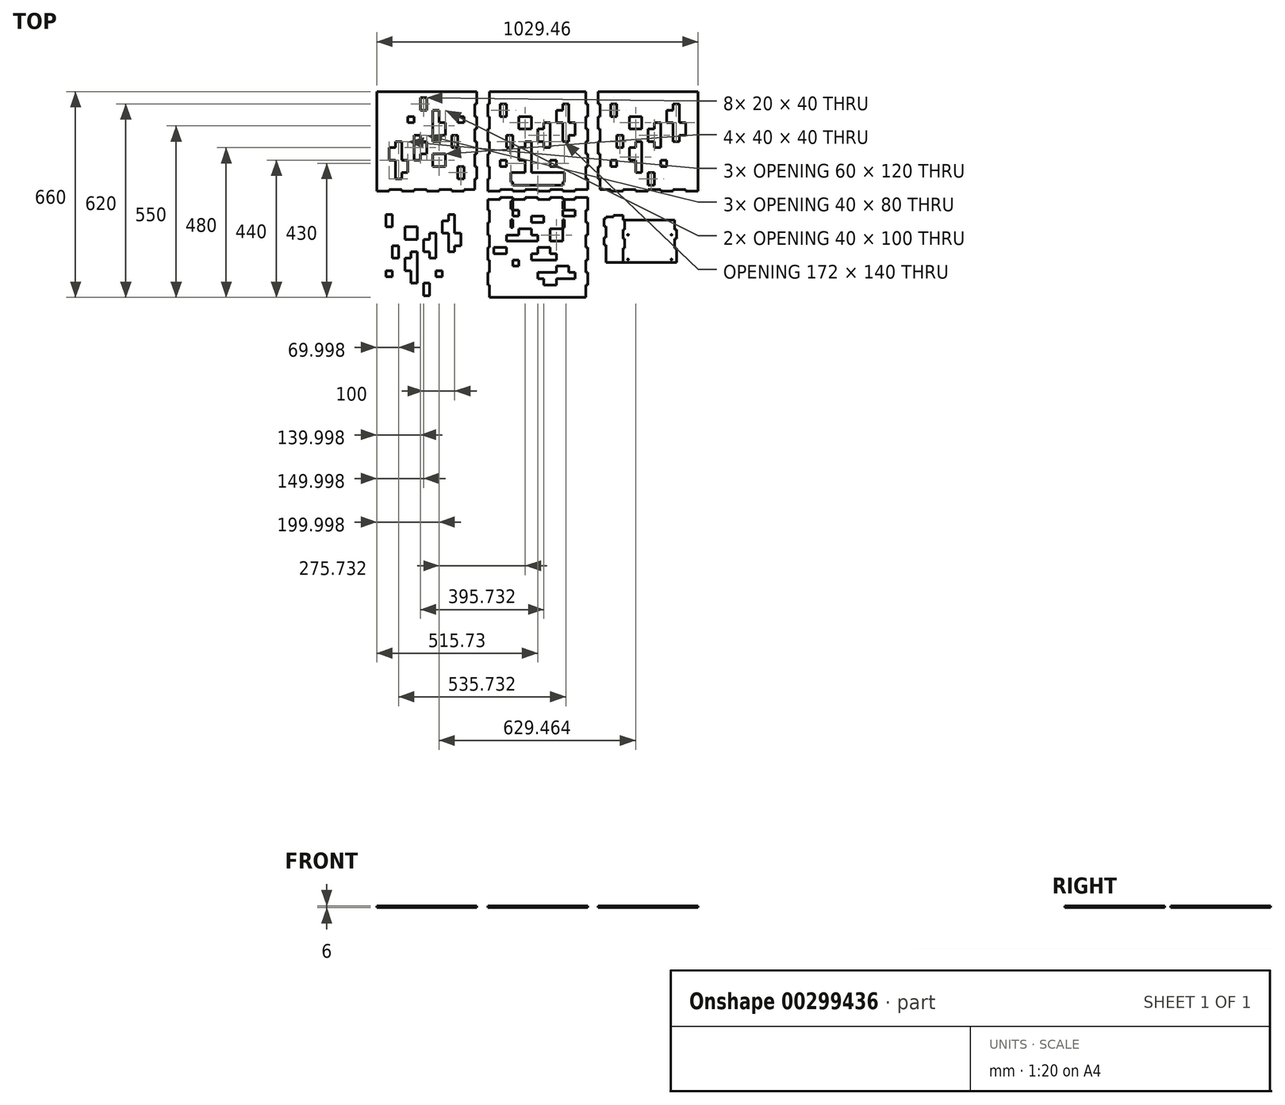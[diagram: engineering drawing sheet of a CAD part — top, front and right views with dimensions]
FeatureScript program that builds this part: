
annotation { "Feature Type Name" : "Feature", "Feature Type Description" : "" }
export const myFeature = defineFeature(function(context is Context, id is Id, definition is map)
    precondition{}
    {
        {
            var Q0;
            Q0=qCreatedBy(makeId("Top.planeOp"),FACE);
            var sketch = newSketch(context, id + "F0", { "sketchPlane" : qUnion([Q0])});
            skLineSegment(sketch, "E0.bottom", {"start": v(0, 0) * mm, "end": v(40, 0) * mm});
            skLineSegment(sketch, "E0.top", {"start": v(6, 320) * mm, "end": v(314, 320) * mm});
            skLineSegment(sketch, "E0.left", {"start": v(0, 0) * mm, "end": v(0, 40) * mm});
            skLineSegment(sketch, "E0.right", {"start": v(320, 6) * mm, "end": v(320, 40) * mm});
            skLineSegment(sketch, "E1.top", {"start": v(40, 6) * mm, "end": v(80, 6) * mm});
            skLineSegment(sketch, "E1.left", {"start": v(40, 0) * mm, "end": v(40, 6) * mm});
            skLineSegment(sketch, "E1.right", {"start": v(80, 0) * mm, "end": v(80, 6) * mm});
            skLineSegment(sketch, "E2.bottom", {"start": v(320, 40) * mm, "end": v(314, 40) * mm});
            skLineSegment(sketch, "E2.top", {"start": v(320, 80) * mm, "end": v(314, 80) * mm});
            skLineSegment(sketch, "E2.right", {"start": v(314, 40) * mm, "end": v(314, 80) * mm});
            skLineSegment(sketch, "E3.0.1.0", {"start": v(320, 160) * mm, "end": v(314, 160) * mm});
            skLineSegment(sketch, "E3.0.1.1", {"start": v(314, 120) * mm, "end": v(314, 160) * mm});
            skLineSegment(sketch, "E3.0.1.2", {"start": v(320, 120) * mm, "end": v(314, 120) * mm});
            skLineSegment(sketch, "E3.0.2.0", {"start": v(320, 240) * mm, "end": v(314, 240) * mm});
            skLineSegment(sketch, "E3.0.2.1", {"start": v(314, 200) * mm, "end": v(314, 240) * mm});
            skLineSegment(sketch, "E3.0.2.2", {"start": v(320, 200) * mm, "end": v(314, 200) * mm});
            skLineSegment(sketch, "E3.0.3.1", {"start": v(314, 280) * mm, "end": v(314, 320) * mm});
            skLineSegment(sketch, "E3.0.3.2", {"start": v(320, 280) * mm, "end": v(314, 280) * mm});
            skLineSegment(sketch, "E3.direction1", {"start": v(314, 80) * mm, "end": v(335.08, 80) * mm, "construction": true});
            skLineSegment(sketch, "E3.direction2", {"start": v(314, 80) * mm, "end": v(314, 160) * mm, "construction": true});
            skLineSegment(sketch, "E4.trimOffspring", {"start": v(320, 80) * mm, "end": v(320, 120) * mm});
            skLineSegment(sketch, "E5.trimOffspring", {"start": v(320, 160) * mm, "end": v(320, 200) * mm});
            skLineSegment(sketch, "E6.trimOffspring", {"start": v(320, 240) * mm, "end": v(320, 280) * mm});
            skLineSegment(sketch, "E7.1.0.0", {"start": v(80, 0) * mm, "end": v(120, 0) * mm});
            skLineSegment(sketch, "E7.1.0.1", {"start": v(120, 6) * mm, "end": v(160, 6) * mm});
            skLineSegment(sketch, "E7.1.0.2", {"start": v(120, 0) * mm, "end": v(120, 6) * mm});
            skLineSegment(sketch, "E7.1.0.3", {"start": v(160, 0) * mm, "end": v(160, 6) * mm});
            skLineSegment(sketch, "E7.2.0.0", {"start": v(160, 0) * mm, "end": v(200, 0) * mm});
            skLineSegment(sketch, "E7.2.0.1", {"start": v(200, 6) * mm, "end": v(240, 6) * mm});
            skLineSegment(sketch, "E7.2.0.2", {"start": v(200, 0) * mm, "end": v(200, 6) * mm});
            skLineSegment(sketch, "E7.2.0.3", {"start": v(240, 0) * mm, "end": v(240, 6) * mm});
            skLineSegment(sketch, "E7.3.0.0", {"start": v(240, 0) * mm, "end": v(280, 0) * mm});
            skLineSegment(sketch, "E7.3.0.1", {"start": v(280, 6) * mm, "end": v(320, 6) * mm});
            skLineSegment(sketch, "E7.3.0.2", {"start": v(280, 0) * mm, "end": v(280, 6) * mm});
            skLineSegment(sketch, "E7.direction1", {"start": v(0, 0) * mm, "end": v(80, 0) * mm, "construction": true});
            skLineSegment(sketch, "E8.bottom", {"start": v(0, 40) * mm, "end": v(6, 40) * mm});
            skLineSegment(sketch, "E8.top", {"start": v(0, 80) * mm, "end": v(6, 80) * mm});
            skLineSegment(sketch, "E8.right", {"start": v(6, 40) * mm, "end": v(6, 80) * mm});
            skLineSegment(sketch, "E9.0.1.0", {"start": v(0, 160) * mm, "end": v(6, 160) * mm});
            skLineSegment(sketch, "E9.0.1.1", {"start": v(6, 120) * mm, "end": v(6, 160) * mm});
            skLineSegment(sketch, "E9.0.1.2", {"start": v(0, 120) * mm, "end": v(6, 120) * mm});
            skLineSegment(sketch, "E9.0.2.0", {"start": v(0, 240) * mm, "end": v(6, 240) * mm});
            skLineSegment(sketch, "E9.0.2.1", {"start": v(6, 200) * mm, "end": v(6, 240) * mm});
            skLineSegment(sketch, "E9.0.2.2", {"start": v(0, 200) * mm, "end": v(6, 200) * mm});
            skLineSegment(sketch, "E9.0.3.1", {"start": v(6, 280) * mm, "end": v(6, 320) * mm});
            skLineSegment(sketch, "E9.0.3.2", {"start": v(0, 280) * mm, "end": v(6, 280) * mm});
            skLineSegment(sketch, "E9.direction1", {"start": v(0, 80) * mm, "end": v(25, 80) * mm, "construction": true});
            skLineSegment(sketch, "E9.direction2", {"start": v(0, 80) * mm, "end": v(0, 120) * mm, "construction": true});
            skLineSegment(sketch, "E10.trimOffspring", {"start": v(0, 240) * mm, "end": v(0, 280) * mm});
            skLineSegment(sketch, "E11.trimOffspring", {"start": v(0, 160) * mm, "end": v(0, 200) * mm});
            skLineSegment(sketch, "E12.trimOffspring", {"start": v(0, 80) * mm, "end": v(0, 120) * mm});
            skSolve(sketch);
        }
        {
            var Q0;
            Q0 = qSketchRegion(id + "F0", true);
            extrude(context, id + "F1", {"entities" : qUnion([Q0]), "depth" : 6 * mm});
        }
        {
            var Q0;
            Q0=makeQuery(id+"F1.opExtrude","SWEPT_BODY",BODY,{"disambiguationData":[OSD([sQuery(id+"F0.wireOp",EDGE,"E0.bottom"),sQuery(id+"F0.wireOp",EDGE,"E0.top"),sQuery(id+"F0.wireOp",EDGE,"E0.left"),sQuery(id+"F0.wireOp",EDGE,"E0.right"),sQuery(id+"F0.wireOp",EDGE,"E1.top"),sQuery(id+"F0.wireOp",EDGE,"E1.left"),sQuery(id+"F0.wireOp",EDGE,"E1.right"),sQuery(id+"F0.wireOp",EDGE,"E2.bottom"),sQuery(id+"F0.wireOp",EDGE,"E2.top"),sQuery(id+"F0.wireOp",EDGE,"E2.right"),sQuery(id+"F0.wireOp",EDGE,"E3.0.1.0"),sQuery(id+"F0.wireOp",EDGE,"E3.0.1.1"),sQuery(id+"F0.wireOp",EDGE,"E3.0.1.2"),sQuery(id+"F0.wireOp",EDGE,"E3.0.2.0"),sQuery(id+"F0.wireOp",EDGE,"E3.0.2.1"),sQuery(id+"F0.wireOp",EDGE,"E3.0.2.2"),sQuery(id+"F0.wireOp",EDGE,"E3.0.3.1"),sQuery(id+"F0.wireOp",EDGE,"E3.0.3.2"),sQuery(id+"F0.wireOp",EDGE,"E4.trimOffspring"),sQuery(id+"F0.wireOp",EDGE,"E5.trimOffspring"),sQuery(id+"F0.wireOp",EDGE,"E6.trimOffspring"),sQuery(id+"F0.wireOp",EDGE,"E7.1.0.0"),sQuery(id+"F0.wireOp",EDGE,"E7.1.0.1"),sQuery(id+"F0.wireOp",EDGE,"E7.1.0.2"),sQuery(id+"F0.wireOp",EDGE,"E7.1.0.3"),sQuery(id+"F0.wireOp",EDGE,"E7.2.0.0"),sQuery(id+"F0.wireOp",EDGE,"E7.2.0.1"),sQuery(id+"F0.wireOp",EDGE,"E7.2.0.2"),sQuery(id+"F0.wireOp",EDGE,"E7.2.0.3"),sQuery(id+"F0.wireOp",EDGE,"E7.3.0.0"),sQuery(id+"F0.wireOp",EDGE,"E7.3.0.1"),sQuery(id+"F0.wireOp",EDGE,"E7.3.0.2"),sQuery(id+"F0.wireOp",EDGE,"E8.bottom"),sQuery(id+"F0.wireOp",EDGE,"E8.top"),sQuery(id+"F0.wireOp",EDGE,"E8.right"),sQuery(id+"F0.wireOp",EDGE,"E9.0.1.0"),sQuery(id+"F0.wireOp",EDGE,"E9.0.1.1"),sQuery(id+"F0.wireOp",EDGE,"E9.0.1.2"),sQuery(id+"F0.wireOp",EDGE,"E9.0.2.0"),sQuery(id+"F0.wireOp",EDGE,"E9.0.2.1"),sQuery(id+"F0.wireOp",EDGE,"E9.0.2.2"),sQuery(id+"F0.wireOp",EDGE,"E9.0.3.1"),sQuery(id+"F0.wireOp",EDGE,"E9.0.3.2"),sQuery(id+"F0.wireOp",EDGE,"E10.trimOffspring"),sQuery(id+"F0.wireOp",EDGE,"E11.trimOffspring"),sQuery(id+"F0.wireOp",EDGE,"E12.trimOffspring")])]});
            var Q1;
            Q1=makeQuery(id+"F1.opExtrude","SWEPT_EDGE",EDGE,{"disambiguationData":[OSD([sQuery(id+"F0.wireOp",EDGE,"E0.bottom"),sQuery(id+"F0.wireOp",EDGE,"E0.left")])]});
            transform(context, id + "F2", {"entities" : qUnion([Q0]), "transformType" : TransformType.ROTATION, "transformAxis" : qUnion([Q1]), "angle" : 180 * degree, "makeCopy" : true});
        }
        {
            var Q0;
            Q0=makeQuery(id+"F2.opPattern","COPY",BODY,{"derivedFrom":makeQuery(id+"F1.opExtrude","SWEPT_BODY",BODY,{"disambiguationData":[OSD([sQuery(id+"F0.wireOp",EDGE,"E0.bottom"),sQuery(id+"F0.wireOp",EDGE,"E0.top"),sQuery(id+"F0.wireOp",EDGE,"E0.left"),sQuery(id+"F0.wireOp",EDGE,"E0.right"),sQuery(id+"F0.wireOp",EDGE,"E1.top"),sQuery(id+"F0.wireOp",EDGE,"E1.left"),sQuery(id+"F0.wireOp",EDGE,"E1.right"),sQuery(id+"F0.wireOp",EDGE,"E2.bottom"),sQuery(id+"F0.wireOp",EDGE,"E2.top"),sQuery(id+"F0.wireOp",EDGE,"E2.right"),sQuery(id+"F0.wireOp",EDGE,"E3.0.1.0"),sQuery(id+"F0.wireOp",EDGE,"E3.0.1.1"),sQuery(id+"F0.wireOp",EDGE,"E3.0.1.2"),sQuery(id+"F0.wireOp",EDGE,"E3.0.2.0"),sQuery(id+"F0.wireOp",EDGE,"E3.0.2.1"),sQuery(id+"F0.wireOp",EDGE,"E3.0.2.2"),sQuery(id+"F0.wireOp",EDGE,"E3.0.3.1"),sQuery(id+"F0.wireOp",EDGE,"E3.0.3.2"),sQuery(id+"F0.wireOp",EDGE,"E4.trimOffspring"),sQuery(id+"F0.wireOp",EDGE,"E5.trimOffspring"),sQuery(id+"F0.wireOp",EDGE,"E6.trimOffspring"),sQuery(id+"F0.wireOp",EDGE,"E7.1.0.0"),sQuery(id+"F0.wireOp",EDGE,"E7.1.0.1"),sQuery(id+"F0.wireOp",EDGE,"E7.1.0.2"),sQuery(id+"F0.wireOp",EDGE,"E7.1.0.3"),sQuery(id+"F0.wireOp",EDGE,"E7.2.0.0"),sQuery(id+"F0.wireOp",EDGE,"E7.2.0.1"),sQuery(id+"F0.wireOp",EDGE,"E7.2.0.2"),sQuery(id+"F0.wireOp",EDGE,"E7.2.0.3"),sQuery(id+"F0.wireOp",EDGE,"E7.3.0.0"),sQuery(id+"F0.wireOp",EDGE,"E7.3.0.1"),sQuery(id+"F0.wireOp",EDGE,"E7.3.0.2"),sQuery(id+"F0.wireOp",EDGE,"E8.bottom"),sQuery(id+"F0.wireOp",EDGE,"E8.top"),sQuery(id+"F0.wireOp",EDGE,"E8.right"),sQuery(id+"F0.wireOp",EDGE,"E9.0.1.0"),sQuery(id+"F0.wireOp",EDGE,"E9.0.1.1"),sQuery(id+"F0.wireOp",EDGE,"E9.0.1.2"),sQuery(id+"F0.wireOp",EDGE,"E9.0.2.0"),sQuery(id+"F0.wireOp",EDGE,"E9.0.2.1"),sQuery(id+"F0.wireOp",EDGE,"E9.0.2.2"),sQuery(id+"F0.wireOp",EDGE,"E9.0.3.1"),sQuery(id+"F0.wireOp",EDGE,"E9.0.3.2"),sQuery(id+"F0.wireOp",EDGE,"E10.trimOffspring"),sQuery(id+"F0.wireOp",EDGE,"E11.trimOffspring"),sQuery(id+"F0.wireOp",EDGE,"E12.trimOffspring")])]}),"instanceName":"1"});
            transform(context, id + "F3", {"entities" : qUnion([Q0]), "transformType" : TransformType.TRANSLATION_3D, "dx" : 320 * mm, "dy" : -20 * mm, "dz" : 0 * mm, "makeCopy" : false});
        }
        {
            var Q0;
            Q0=makeQuery(id+"F1.opExtrude","CAP_FACE",FACE,{"disambiguationData":[OSD([sQuery(id+"F0.wireOp",EDGE,"E0.bottom"),sQuery(id+"F0.wireOp",EDGE,"E0.top"),sQuery(id+"F0.wireOp",EDGE,"E0.left"),sQuery(id+"F0.wireOp",EDGE,"E0.right"),sQuery(id+"F0.wireOp",EDGE,"E1.top"),sQuery(id+"F0.wireOp",EDGE,"E1.left"),sQuery(id+"F0.wireOp",EDGE,"E1.right"),sQuery(id+"F0.wireOp",EDGE,"E2.bottom"),sQuery(id+"F0.wireOp",EDGE,"E2.top"),sQuery(id+"F0.wireOp",EDGE,"E2.right"),sQuery(id+"F0.wireOp",EDGE,"E3.0.1.0"),sQuery(id+"F0.wireOp",EDGE,"E3.0.1.1"),sQuery(id+"F0.wireOp",EDGE,"E3.0.1.2"),sQuery(id+"F0.wireOp",EDGE,"E3.0.2.0"),sQuery(id+"F0.wireOp",EDGE,"E3.0.2.1"),sQuery(id+"F0.wireOp",EDGE,"E3.0.2.2"),sQuery(id+"F0.wireOp",EDGE,"E3.0.3.1"),sQuery(id+"F0.wireOp",EDGE,"E3.0.3.2"),sQuery(id+"F0.wireOp",EDGE,"E4.trimOffspring"),sQuery(id+"F0.wireOp",EDGE,"E5.trimOffspring"),sQuery(id+"F0.wireOp",EDGE,"E6.trimOffspring"),sQuery(id+"F0.wireOp",EDGE,"E7.1.0.0"),sQuery(id+"F0.wireOp",EDGE,"E7.1.0.1"),sQuery(id+"F0.wireOp",EDGE,"E7.1.0.2"),sQuery(id+"F0.wireOp",EDGE,"E7.1.0.3"),sQuery(id+"F0.wireOp",EDGE,"E7.2.0.0"),sQuery(id+"F0.wireOp",EDGE,"E7.2.0.1"),sQuery(id+"F0.wireOp",EDGE,"E7.2.0.2"),sQuery(id+"F0.wireOp",EDGE,"E7.2.0.3"),sQuery(id+"F0.wireOp",EDGE,"E7.3.0.0"),sQuery(id+"F0.wireOp",EDGE,"E7.3.0.1"),sQuery(id+"F0.wireOp",EDGE,"E7.3.0.2"),sQuery(id+"F0.wireOp",EDGE,"E8.bottom"),sQuery(id+"F0.wireOp",EDGE,"E8.top"),sQuery(id+"F0.wireOp",EDGE,"E8.right"),sQuery(id+"F0.wireOp",EDGE,"E9.0.1.0"),sQuery(id+"F0.wireOp",EDGE,"E9.0.1.1"),sQuery(id+"F0.wireOp",EDGE,"E9.0.1.2"),sQuery(id+"F0.wireOp",EDGE,"E9.0.2.0"),sQuery(id+"F0.wireOp",EDGE,"E9.0.2.1"),sQuery(id+"F0.wireOp",EDGE,"E9.0.2.2"),sQuery(id+"F0.wireOp",EDGE,"E9.0.3.1"),sQuery(id+"F0.wireOp",EDGE,"E9.0.3.2"),sQuery(id+"F0.wireOp",EDGE,"E10.trimOffspring"),sQuery(id+"F0.wireOp",EDGE,"E11.trimOffspring"),sQuery(id+"F0.wireOp",EDGE,"E12.trimOffspring")])],"isStart":false});
            var sketch = newSketch(context, id + "F4", { "sketchPlane" : qUnion([Q0])});
            skLineSegment(sketch, "E13", {"start": v(160, 320) * mm, "end": v(160, 6) * mm, "construction": true});
            skLineSegment(sketch, "E14.bottom", {"start": v(74, 60) * mm, "end": v(80, 60) * mm});
            skLineSegment(sketch, "E14.top", {"start": v(74, 30) * mm, "end": v(80, 30) * mm});
            skLineSegment(sketch, "E14.left", {"start": v(74, 60) * mm, "end": v(74, 30) * mm});
            skLineSegment(sketch, "E14.right", {"start": v(80, 60) * mm, "end": v(80, 30) * mm});
            skLineSegment(sketch, "E15.MirrorCS", {"start": v(246, 60) * mm, "end": v(240, 60) * mm});
            skLineSegment(sketch, "E16.MirrorCS", {"start": v(246, 60) * mm, "end": v(246, 30) * mm});
            skLineSegment(sketch, "E17.MirrorCS", {"start": v(246, 30) * mm, "end": v(240, 30) * mm});
            skLineSegment(sketch, "E18.MirrorCS", {"start": v(240, 60) * mm, "end": v(240, 30) * mm});
            skLineSegment(sketch, "E19.bottom", {"start": v(74, -31) * mm, "end": v(80, -31) * mm});
            skLineSegment(sketch, "E19.top", {"start": v(74, -56) * mm, "end": v(80, -56) * mm});
            skLineSegment(sketch, "E19.left", {"start": v(74, -31) * mm, "end": v(74, -56) * mm});
            skLineSegment(sketch, "E19.right", {"start": v(80, -31) * mm, "end": v(80, -56) * mm});
            skLineSegment(sketch, "E20", {"start": v(6, -166) * mm, "end": v(314, -166) * mm, "construction": true});
            skLineSegment(sketch, "E21.0.1.0", {"start": v(74, -116) * mm, "end": v(80, -116) * mm});
            skLineSegment(sketch, "E21.0.1.1", {"start": v(80, -91) * mm, "end": v(80, -116) * mm});
            skLineSegment(sketch, "E21.0.1.2", {"start": v(74, -91) * mm, "end": v(80, -91) * mm});
            skLineSegment(sketch, "E21.0.1.3", {"start": v(74, -91) * mm, "end": v(74, -116) * mm});
            skLineSegment(sketch, "E21.direction1", {"start": v(74, -56) * mm, "end": v(103, -56) * mm, "construction": true});
            skLineSegment(sketch, "E21.direction2", {"start": v(74, -56) * mm, "end": v(74, -116) * mm, "construction": true});
            skLineSegment(sketch, "E22.MirrorCS", {"start": v(246, -116) * mm, "end": v(240, -116) * mm});
            skLineSegment(sketch, "E23.MirrorCS", {"start": v(246, -91) * mm, "end": v(240, -91) * mm});
            skLineSegment(sketch, "E24.MirrorCS", {"start": v(240, -91) * mm, "end": v(240, -116) * mm});
            skLineSegment(sketch, "E25.MirrorCS", {"start": v(246, -91) * mm, "end": v(246, -116) * mm});
            skLineSegment(sketch, "E26.MirrorCS", {"start": v(246, -56) * mm, "end": v(240, -56) * mm});
            skLineSegment(sketch, "E27.MirrorCS", {"start": v(246, -31) * mm, "end": v(240, -31) * mm});
            skLineSegment(sketch, "E28.MirrorCS", {"start": v(246, -31) * mm, "end": v(246, -56) * mm});
            skLineSegment(sketch, "E29.MirrorCS", {"start": v(240, -31) * mm, "end": v(240, -56) * mm});
            skLineSegment(sketch, "E30.bottom", {"start": v(80, 60) * mm, "end": v(240, 60) * mm});
            skLineSegment(sketch, "E30.top", {"start": v(80, 20) * mm, "end": v(240, 20) * mm});
            skLineSegment(sketch, "E30.left", {"start": v(80, 60) * mm, "end": v(80, 20) * mm});
            skLineSegment(sketch, "E30.right", {"start": v(240, 60) * mm, "end": v(240, 20) * mm});
            skSolve(sketch);
        }
        {
            var Q0;
            Q0 = qSketchRegion(id + "F4", true);
            extrude(context, id + "F5", {"entities" : qUnion([Q0]), "operationType" : NewBodyOperationType.REMOVE, "endBound" : BoundingType.THROUGH_ALL, "oppositeDirection" : true, "depth" : 25 * mm});
        }
        {
            var Q0;
            Q0=makeQuery(id+"F4.imprint","IMPRINT",FACE,{"disambiguationData":[TD([[makeQuery(id+"F4.imprint","IMPRINT",EDGE,{"derivedFrom":sQuery(id+"F4.wireOp",EDGE,"E19.bottom")}),-1.0]])]});
            var Q1;
            Q1=makeQuery(id+"F4.imprint","IMPRINT",FACE,{"disambiguationData":[TD([[makeQuery(id+"F4.imprint","IMPRINT",EDGE,{"derivedFrom":sQuery(id+"F4.wireOp",EDGE,"E26.MirrorCS")}),-1.0]])]});
            var Q2;
            Q2=makeQuery(id+"F4.imprint","IMPRINT",FACE,{"disambiguationData":[TD([[makeQuery(id+"F4.imprint","IMPRINT",EDGE,{"derivedFrom":sQuery(id+"F4.wireOp",EDGE,"E21.0.1.0")}),1.0]])]});
            var Q3;
            Q3=makeQuery(id+"F4.imprint","IMPRINT",FACE,{"disambiguationData":[TD([[makeQuery(id+"F4.imprint","IMPRINT",EDGE,{"derivedFrom":sQuery(id+"F4.wireOp",EDGE,"E22.MirrorCS")}),-1.0]])]});
            extrude(context, id + "F6", {"entities" : qUnion([Q0, Q1, Q2, Q3]), "operationType" : NewBodyOperationType.REMOVE, "endBound" : BoundingType.THROUGH_ALL, "oppositeDirection" : true, "depth" : 25 * mm});
        }
        {
            var Q0;
            Q0=qCreatedBy(makeId("Top.planeOp"),FACE);
            var sketch = newSketch(context, id + "F7", { "sketchPlane" : qUnion([Q0])});
            skLineSegment(sketch, "E31.bottom", {"start": v(378.9, -82.37) * mm, "end": v(402.9, -82.37) * mm});
            skLineSegment(sketch, "E31.top", {"start": v(378.9, -227.37) * mm, "end": v(432.9, -227.37) * mm});
            skLineSegment(sketch, "E31.left", {"start": v(378.9, -82.37) * mm, "end": v(378.9, -87.37) * mm});
            skLineSegment(sketch, "E31.right", {"start": v(432.9, -76.37) * mm, "end": v(432.9, -92.37) * mm});
            skLineSegment(sketch, "E32.bottom", {"start": v(378.9, -87.37) * mm, "end": v(372.9, -87.37) * mm});
            skLineSegment(sketch, "E32.top", {"start": v(378.9, -112.37) * mm, "end": v(372.9, -112.37) * mm});
            skLineSegment(sketch, "E32.right", {"start": v(372.9, -87.37) * mm, "end": v(372.9, -112.37) * mm});
            skLineSegment(sketch, "E33.top", {"start": v(432.9, -76.37) * mm, "end": v(402.9, -76.37) * mm});
            skLineSegment(sketch, "E33.right", {"start": v(402.9, -82.37) * mm, "end": v(402.9, -76.37) * mm});
            skLineSegment(sketch, "E34.0.1.0", {"start": v(378.9, -172.37) * mm, "end": v(372.9, -172.37) * mm});
            skLineSegment(sketch, "E34.0.1.1", {"start": v(372.9, -147.37) * mm, "end": v(372.9, -172.37) * mm});
            skLineSegment(sketch, "E34.0.1.2", {"start": v(378.9, -147.37) * mm, "end": v(372.9, -147.37) * mm});
            skLineSegment(sketch, "E34.direction1", {"start": v(372.9, -112.37) * mm, "end": v(386.62, -112.37) * mm, "construction": true});
            skLineSegment(sketch, "E34.direction2", {"start": v(372.9, -112.37) * mm, "end": v(372.9, -172.37) * mm, "construction": true});
            skLineSegment(sketch, "E35.trimOffspring", {"start": v(378.9, -112.37) * mm, "end": v(378.9, -147.37) * mm});
            skLineSegment(sketch, "E36.trimOffspring", {"start": v(378.9, -172.37) * mm, "end": v(378.9, -227.37) * mm});
            skLineSegment(sketch, "E37.bottom", {"start": v(432.9, -92.37) * mm, "end": v(438.9, -92.37) * mm});
            skLineSegment(sketch, "E37.top", {"start": v(432.9, -122.37) * mm, "end": v(438.9, -122.37) * mm});
            skLineSegment(sketch, "E37.right", {"start": v(438.9, -92.37) * mm, "end": v(438.9, -122.37) * mm});
            skLineSegment(sketch, "E38.0.1.0", {"start": v(432.9, -152.37) * mm, "end": v(438.9, -152.37) * mm});
            skLineSegment(sketch, "E38.0.1.1", {"start": v(438.9, -152.37) * mm, "end": v(438.9, -182.37) * mm});
            skLineSegment(sketch, "E38.0.1.2", {"start": v(432.9, -182.37) * mm, "end": v(438.9, -182.37) * mm});
            skLineSegment(sketch, "E38.direction2", {"start": v(432.9, -122.37) * mm, "end": v(432.9, -152.37) * mm, "construction": true});
            skLineSegment(sketch, "E39.trimOffspring", {"start": v(432.9, -182.37) * mm, "end": v(432.9, -227.37) * mm});
            skLineSegment(sketch, "E40.trimOffspring", {"start": v(432.9, -122.37) * mm, "end": v(432.9, -152.37) * mm});
            skLineSegment(sketch, "E41", {"start": v(432.9, -227.37) * mm, "end": v(518.9, -227.37) * mm});
            skLineSegment(sketch, "E42", {"start": v(518.9, -92.37) * mm, "end": v(518.9, -227.37) * mm, "construction": true});
            skLineSegment(sketch, "E43.MirrorCS", {"start": v(604.9, -182.37) * mm, "end": v(598.9, -182.37) * mm});
            skLineSegment(sketch, "E44.MirrorCS", {"start": v(604.9, -122.37) * mm, "end": v(598.9, -122.37) * mm});
            skLineSegment(sketch, "E45.MirrorCS", {"start": v(604.9, -152.37) * mm, "end": v(598.9, -152.37) * mm});
            skLineSegment(sketch, "E46.MirrorCS", {"start": v(604.9, -122.37) * mm, "end": v(604.9, -152.37) * mm});
            skLineSegment(sketch, "E47.MirrorCS", {"start": v(598.9, -152.37) * mm, "end": v(598.9, -182.37) * mm});
            skLineSegment(sketch, "E48.MirrorCS", {"start": v(604.9, -182.37) * mm, "end": v(604.9, -227.37) * mm});
            skLineSegment(sketch, "E49.MirrorCS", {"start": v(604.9, -122.37) * mm, "end": v(604.9, -152.37) * mm, "construction": true});
            skLineSegment(sketch, "E50.MirrorCS", {"start": v(598.9, -92.37) * mm, "end": v(598.9, -122.37) * mm});
            skLineSegment(sketch, "E51.MirrorCS", {"start": v(604.9, -227.37) * mm, "end": v(518.9, -227.37) * mm});
            skPoint(sketch, "E52", {"position": v(449.2, -139.37) * mm});
            skPoint(sketch, "E53.MirrorP", {"position": v(588.6, -139.37) * mm});
            skPoint(sketch, "E54", {"position": v(449.2, -218.37) * mm});
            skPoint(sketch, "E55.MirrorP", {"position": v(588.6, -218.37) * mm});
            skLineSegment(sketch, "E56", {"start": v(438.9, -92.37) * mm, "end": v(598.9, -92.37) * mm});
            skSolve(sketch);
        }
        {
            var Q0;
            Q0=makeQuery(id+"F7.imprint","IMPRINT",FACE,{"disambiguationData":[TD([[makeQuery(id+"F7.imprint","IMPRINT",EDGE,{"derivedFrom":sQuery(id+"F7.wireOp",EDGE,"E31.bottom")}),-1.0]])]});
            extrude(context, id + "F8", {"entities" : qUnion([Q0]), "depth" : 6 * mm});
        }
        {
            var Q0;
            Q0=makeQuery(id+"F7.imprint","IMPRINT",FACE,{"disambiguationData":[TD([[makeQuery(id+"F7.imprint","IMPRINT",EDGE,{"derivedFrom":sQuery(id+"F7.wireOp",EDGE,"E37.top")}),-1.0]])]});
            extrude(context, id + "F9", {"entities" : qUnion([Q0]), "depth" : 6 * mm});
        }
        {
            var Q0;
            Q0=sQuery(id+"F7.wireOp",VERTEX,"E52");
            var Q1;
            Q1=sQuery(id+"F7.wireOp",VERTEX,"E53.MirrorP");
            var Q2;
            Q2=sQuery(id+"F7.wireOp",VERTEX,"E54");
            var Q3;
            Q3=sQuery(id+"F7.wireOp",VERTEX,"E55.MirrorP");
            var Q4;
            Q4=makeQuery(id+"F9.opExtrude","SWEPT_BODY",BODY,{"disambiguationData":[OSD([sQuery(id+"F7.wireOp",EDGE,"E31.right"),sQuery(id+"F7.wireOp",EDGE,"E37.bottom"),sQuery(id+"F7.wireOp",EDGE,"E37.top"),sQuery(id+"F7.wireOp",EDGE,"E37.right"),sQuery(id+"F7.wireOp",EDGE,"E38.0.1.0"),sQuery(id+"F7.wireOp",EDGE,"E38.0.1.1"),sQuery(id+"F7.wireOp",EDGE,"E38.0.1.2"),sQuery(id+"F7.wireOp",EDGE,"E39.trimOffspring"),sQuery(id+"F7.wireOp",EDGE,"E40.trimOffspring"),sQuery(id+"F7.wireOp",EDGE,"jgh2MYiH-jTgE-0Iw7-kaac-s1TBbCvIartK"),sQuery(id+"F7.wireOp",EDGE,"E41"),sQuery(id+"F7.wireOp",EDGE,"de06030a-5946-498d-ad5b-0ab8e06975840.MirrorCS"),sQuery(id+"F7.wireOp",EDGE,"E43.MirrorCS"),sQuery(id+"F7.wireOp",EDGE,"E44.MirrorCS"),sQuery(id+"F7.wireOp",EDGE,"e7224b58-42de-4460-80b3-c9ff548c79182.MirrorCS"),sQuery(id+"F7.wireOp",EDGE,"E45.MirrorCS"),sQuery(id+"F7.wireOp",EDGE,"E46.MirrorCS"),sQuery(id+"F7.wireOp",EDGE,"E47.MirrorCS"),sQuery(id+"F7.wireOp",EDGE,"E48.MirrorCS"),sQuery(id+"F7.wireOp",EDGE,"e7224b58-42de-4460-80b3-c9ff548c79189.MirrorCS"),sQuery(id+"F7.wireOp",EDGE,"E50.MirrorCS"),sQuery(id+"F7.wireOp",EDGE,"E51.MirrorCS")])]});
            hole(context, id + "F10", {"style" : HoleStyle.SIMPLE, "endStyle" : HoleEndStyle.THROUGH, "oppositeDirection" : true, "standardTappedOrClearance" : lookupTablePath({ "standard" : "ISO", "fit" : "Normal", "size" : "M3", "type" : "Clearance" }), "standardBlindInLast" : lookupTablePath({ "fit" : "Standard", "standard" : "ISO", "size" : "M3", "type" : "Clearance" }), "holeDiameter" : 3.3 * mm, "tappedDepth" : 6 * mm, "tapClearance" : 3, "locations" : qUnion([Q0, Q1, Q2, Q3]), "scope" : qUnion([Q4])});
        }
        {
            var Q0;
            Q0=makeQuery(id+"F1.opExtrude","CAP_FACE",FACE,{"disambiguationData":[OSD([sQuery(id+"F0.wireOp",EDGE,"E0.bottom"),sQuery(id+"F0.wireOp",EDGE,"E0.top"),sQuery(id+"F0.wireOp",EDGE,"E0.left"),sQuery(id+"F0.wireOp",EDGE,"E0.right"),sQuery(id+"F0.wireOp",EDGE,"E1.top"),sQuery(id+"F0.wireOp",EDGE,"E1.left"),sQuery(id+"F0.wireOp",EDGE,"E1.right"),sQuery(id+"F0.wireOp",EDGE,"E2.bottom"),sQuery(id+"F0.wireOp",EDGE,"E2.top"),sQuery(id+"F0.wireOp",EDGE,"E2.right"),sQuery(id+"F0.wireOp",EDGE,"E3.0.1.0"),sQuery(id+"F0.wireOp",EDGE,"E3.0.1.1"),sQuery(id+"F0.wireOp",EDGE,"E3.0.1.2"),sQuery(id+"F0.wireOp",EDGE,"E3.0.2.0"),sQuery(id+"F0.wireOp",EDGE,"E3.0.2.1"),sQuery(id+"F0.wireOp",EDGE,"E3.0.2.2"),sQuery(id+"F0.wireOp",EDGE,"E3.0.3.1"),sQuery(id+"F0.wireOp",EDGE,"E3.0.3.2"),sQuery(id+"F0.wireOp",EDGE,"E4.trimOffspring"),sQuery(id+"F0.wireOp",EDGE,"E5.trimOffspring"),sQuery(id+"F0.wireOp",EDGE,"E6.trimOffspring"),sQuery(id+"F0.wireOp",EDGE,"E7.1.0.0"),sQuery(id+"F0.wireOp",EDGE,"E7.1.0.1"),sQuery(id+"F0.wireOp",EDGE,"E7.1.0.2"),sQuery(id+"F0.wireOp",EDGE,"E7.1.0.3"),sQuery(id+"F0.wireOp",EDGE,"E7.2.0.0"),sQuery(id+"F0.wireOp",EDGE,"E7.2.0.1"),sQuery(id+"F0.wireOp",EDGE,"E7.2.0.2"),sQuery(id+"F0.wireOp",EDGE,"E7.2.0.3"),sQuery(id+"F0.wireOp",EDGE,"E7.3.0.0"),sQuery(id+"F0.wireOp",EDGE,"E7.3.0.1"),sQuery(id+"F0.wireOp",EDGE,"E7.3.0.2"),sQuery(id+"F0.wireOp",EDGE,"E8.bottom"),sQuery(id+"F0.wireOp",EDGE,"E8.top"),sQuery(id+"F0.wireOp",EDGE,"E8.right"),sQuery(id+"F0.wireOp",EDGE,"E9.0.1.0"),sQuery(id+"F0.wireOp",EDGE,"E9.0.1.1"),sQuery(id+"F0.wireOp",EDGE,"E9.0.1.2"),sQuery(id+"F0.wireOp",EDGE,"E9.0.2.0"),sQuery(id+"F0.wireOp",EDGE,"E9.0.2.1"),sQuery(id+"F0.wireOp",EDGE,"E9.0.2.2"),sQuery(id+"F0.wireOp",EDGE,"E9.0.3.1"),sQuery(id+"F0.wireOp",EDGE,"E9.0.3.2"),sQuery(id+"F0.wireOp",EDGE,"E10.trimOffspring"),sQuery(id+"F0.wireOp",EDGE,"E11.trimOffspring"),sQuery(id+"F0.wireOp",EDGE,"E12.trimOffspring")])],"isStart":false});
            var sketch = newSketch(context, id + "F11", { "sketchPlane" : qUnion([Q0])});
            skPoint(sketch, "E57", {"position": v(20, 20) * mm});
            skPoint(sketch, "E58.0.1.0", {"position": v(20, 40) * mm});
            skPoint(sketch, "E58.0.2.0", {"position": v(20, 60) * mm});
            skPoint(sketch, "E58.0.3.0", {"position": v(20, 80) * mm});
            skPoint(sketch, "E58.0.4.0", {"position": v(20, 100) * mm});
            skPoint(sketch, "E58.0.5.0", {"position": v(20, 120) * mm});
            skPoint(sketch, "E58.0.6.0", {"position": v(20, 140) * mm});
            skPoint(sketch, "E58.0.7.0", {"position": v(20, 160) * mm});
            skPoint(sketch, "E58.0.8.0", {"position": v(20, 180) * mm});
            skPoint(sketch, "E58.0.9.0", {"position": v(20, 200) * mm});
            skPoint(sketch, "E58.0.10.0", {"position": v(20, 220) * mm});
            skPoint(sketch, "E58.0.11.0", {"position": v(20, 240) * mm});
            skPoint(sketch, "E58.0.12.0", {"position": v(20, 260) * mm});
            skPoint(sketch, "E58.0.13.0", {"position": v(20, 280) * mm});
            skPoint(sketch, "E58.1.0.0", {"position": v(40, 20) * mm});
            skPoint(sketch, "E58.1.1.0", {"position": v(40, 40) * mm});
            skPoint(sketch, "E58.1.2.0", {"position": v(40, 60) * mm});
            skPoint(sketch, "E58.1.3.0", {"position": v(40, 80) * mm});
            skPoint(sketch, "E58.1.4.0", {"position": v(40, 100) * mm});
            skPoint(sketch, "E58.1.5.0", {"position": v(40, 120) * mm});
            skPoint(sketch, "E58.1.6.0", {"position": v(40, 140) * mm});
            skPoint(sketch, "E58.1.7.0", {"position": v(40, 160) * mm});
            skPoint(sketch, "E58.1.8.0", {"position": v(40, 180) * mm});
            skPoint(sketch, "E58.1.9.0", {"position": v(40, 200) * mm});
            skPoint(sketch, "E58.1.10.0", {"position": v(40, 220) * mm});
            skPoint(sketch, "E58.1.11.0", {"position": v(40, 240) * mm});
            skPoint(sketch, "E58.1.12.0", {"position": v(40, 260) * mm});
            skPoint(sketch, "E58.1.13.0", {"position": v(40, 280) * mm});
            skPoint(sketch, "E58.2.0.0", {"position": v(60, 20) * mm});
            skPoint(sketch, "E58.2.1.0", {"position": v(60, 40) * mm});
            skPoint(sketch, "E58.2.2.0", {"position": v(60, 60) * mm});
            skPoint(sketch, "E58.2.3.0", {"position": v(60, 80) * mm});
            skPoint(sketch, "E58.2.4.0", {"position": v(60, 100) * mm});
            skPoint(sketch, "E58.2.5.0", {"position": v(60, 120) * mm});
            skPoint(sketch, "E58.2.6.0", {"position": v(60, 140) * mm});
            skPoint(sketch, "E58.2.7.0", {"position": v(60, 160) * mm});
            skPoint(sketch, "E58.2.8.0", {"position": v(60, 180) * mm});
            skPoint(sketch, "E58.2.9.0", {"position": v(60, 200) * mm});
            skPoint(sketch, "E58.2.10.0", {"position": v(60, 220) * mm});
            skPoint(sketch, "E58.2.11.0", {"position": v(60, 240) * mm});
            skPoint(sketch, "E58.2.12.0", {"position": v(60, 260) * mm});
            skPoint(sketch, "E58.2.13.0", {"position": v(60, 280) * mm});
            skPoint(sketch, "E58.3.0.0", {"position": v(80, 20) * mm});
            skPoint(sketch, "E58.3.1.0", {"position": v(80, 40) * mm});
            skPoint(sketch, "E58.3.2.0", {"position": v(80, 60) * mm});
            skPoint(sketch, "E58.3.3.0", {"position": v(80, 80) * mm});
            skPoint(sketch, "E58.3.4.0", {"position": v(80, 100) * mm});
            skPoint(sketch, "E58.3.5.0", {"position": v(80, 120) * mm});
            skPoint(sketch, "E58.3.6.0", {"position": v(80, 140) * mm});
            skPoint(sketch, "E58.3.7.0", {"position": v(80, 160) * mm});
            skPoint(sketch, "E58.3.8.0", {"position": v(80, 180) * mm});
            skPoint(sketch, "E58.3.9.0", {"position": v(80, 200) * mm});
            skPoint(sketch, "E58.3.10.0", {"position": v(80, 220) * mm});
            skPoint(sketch, "E58.3.11.0", {"position": v(80, 240) * mm});
            skPoint(sketch, "E58.3.12.0", {"position": v(80, 260) * mm});
            skPoint(sketch, "E58.3.13.0", {"position": v(80, 280) * mm});
            skPoint(sketch, "E58.4.0.0", {"position": v(100, 20) * mm});
            skPoint(sketch, "E58.4.1.0", {"position": v(100, 40) * mm});
            skPoint(sketch, "E58.4.2.0", {"position": v(100, 60) * mm});
            skPoint(sketch, "E58.4.3.0", {"position": v(100, 80) * mm});
            skPoint(sketch, "E58.4.4.0", {"position": v(100, 100) * mm});
            skPoint(sketch, "E58.4.5.0", {"position": v(100, 120) * mm});
            skPoint(sketch, "E58.4.6.0", {"position": v(100, 140) * mm});
            skPoint(sketch, "E58.4.7.0", {"position": v(100, 160) * mm});
            skPoint(sketch, "E58.4.8.0", {"position": v(100, 180) * mm});
            skPoint(sketch, "E58.4.9.0", {"position": v(100, 200) * mm});
            skPoint(sketch, "E58.4.10.0", {"position": v(100, 220) * mm});
            skPoint(sketch, "E58.4.11.0", {"position": v(100, 240) * mm});
            skPoint(sketch, "E58.4.12.0", {"position": v(100, 260) * mm});
            skPoint(sketch, "E58.4.13.0", {"position": v(100, 280) * mm});
            skPoint(sketch, "E58.5.0.0", {"position": v(120, 20) * mm});
            skPoint(sketch, "E58.5.1.0", {"position": v(120, 40) * mm});
            skPoint(sketch, "E58.5.2.0", {"position": v(120, 60) * mm});
            skPoint(sketch, "E58.5.3.0", {"position": v(120, 80) * mm});
            skPoint(sketch, "E58.5.4.0", {"position": v(120, 100) * mm});
            skPoint(sketch, "E58.5.5.0", {"position": v(120, 120) * mm});
            skPoint(sketch, "E58.5.6.0", {"position": v(120, 140) * mm});
            skPoint(sketch, "E58.5.7.0", {"position": v(120, 160) * mm});
            skPoint(sketch, "E58.5.8.0", {"position": v(120, 180) * mm});
            skPoint(sketch, "E58.5.9.0", {"position": v(120, 200) * mm});
            skPoint(sketch, "E58.5.10.0", {"position": v(120, 220) * mm});
            skPoint(sketch, "E58.5.11.0", {"position": v(120, 240) * mm});
            skPoint(sketch, "E58.5.12.0", {"position": v(120, 260) * mm});
            skPoint(sketch, "E58.5.13.0", {"position": v(120, 280) * mm});
            skPoint(sketch, "E58.6.0.0", {"position": v(140, 20) * mm});
            skPoint(sketch, "E58.6.1.0", {"position": v(140, 40) * mm});
            skPoint(sketch, "E58.6.2.0", {"position": v(140, 60) * mm});
            skPoint(sketch, "E58.6.3.0", {"position": v(140, 80) * mm});
            skPoint(sketch, "E58.6.4.0", {"position": v(140, 100) * mm});
            skPoint(sketch, "E58.6.5.0", {"position": v(140, 120) * mm});
            skPoint(sketch, "E58.6.6.0", {"position": v(140, 140) * mm});
            skPoint(sketch, "E58.6.7.0", {"position": v(140, 160) * mm});
            skPoint(sketch, "E58.6.8.0", {"position": v(140, 180) * mm});
            skPoint(sketch, "E58.6.9.0", {"position": v(140, 200) * mm});
            skPoint(sketch, "E58.6.10.0", {"position": v(140, 220) * mm});
            skPoint(sketch, "E58.6.11.0", {"position": v(140, 240) * mm});
            skPoint(sketch, "E58.6.12.0", {"position": v(140, 260) * mm});
            skPoint(sketch, "E58.6.13.0", {"position": v(140, 280) * mm});
            skPoint(sketch, "E58.7.0.0", {"position": v(160, 20) * mm});
            skPoint(sketch, "E58.7.1.0", {"position": v(160, 40) * mm});
            skPoint(sketch, "E58.7.2.0", {"position": v(160, 60) * mm});
            skPoint(sketch, "E58.7.3.0", {"position": v(160, 80) * mm});
            skPoint(sketch, "E58.7.4.0", {"position": v(160, 100) * mm});
            skPoint(sketch, "E58.7.5.0", {"position": v(160, 120) * mm});
            skPoint(sketch, "E58.7.6.0", {"position": v(160, 140) * mm});
            skPoint(sketch, "E58.7.7.0", {"position": v(160, 160) * mm});
            skPoint(sketch, "E58.7.8.0", {"position": v(160, 180) * mm});
            skPoint(sketch, "E58.7.9.0", {"position": v(160, 200) * mm});
            skPoint(sketch, "E58.7.10.0", {"position": v(160, 220) * mm});
            skPoint(sketch, "E58.7.11.0", {"position": v(160, 240) * mm});
            skPoint(sketch, "E58.7.12.0", {"position": v(160, 260) * mm});
            skPoint(sketch, "E58.7.13.0", {"position": v(160, 280) * mm});
            skPoint(sketch, "E58.8.0.0", {"position": v(180, 20) * mm});
            skPoint(sketch, "E58.8.1.0", {"position": v(180, 40) * mm});
            skPoint(sketch, "E58.8.2.0", {"position": v(180, 60) * mm});
            skPoint(sketch, "E58.8.3.0", {"position": v(180, 80) * mm});
            skPoint(sketch, "E58.8.4.0", {"position": v(180, 100) * mm});
            skPoint(sketch, "E58.8.5.0", {"position": v(180, 120) * mm});
            skPoint(sketch, "E58.8.6.0", {"position": v(180, 140) * mm});
            skPoint(sketch, "E58.8.7.0", {"position": v(180, 160) * mm});
            skPoint(sketch, "E58.8.8.0", {"position": v(180, 180) * mm});
            skPoint(sketch, "E58.8.9.0", {"position": v(180, 200) * mm});
            skPoint(sketch, "E58.8.10.0", {"position": v(180, 220) * mm});
            skPoint(sketch, "E58.8.11.0", {"position": v(180, 240) * mm});
            skPoint(sketch, "E58.8.12.0", {"position": v(180, 260) * mm});
            skPoint(sketch, "E58.8.13.0", {"position": v(180, 280) * mm});
            skPoint(sketch, "E58.9.0.0", {"position": v(200, 20) * mm});
            skPoint(sketch, "E58.9.1.0", {"position": v(200, 40) * mm});
            skPoint(sketch, "E58.9.2.0", {"position": v(200, 60) * mm});
            skPoint(sketch, "E58.9.3.0", {"position": v(200, 80) * mm});
            skPoint(sketch, "E58.9.4.0", {"position": v(200, 100) * mm});
            skPoint(sketch, "E58.9.5.0", {"position": v(200, 120) * mm});
            skPoint(sketch, "E58.9.6.0", {"position": v(200, 140) * mm});
            skPoint(sketch, "E58.9.7.0", {"position": v(200, 160) * mm});
            skPoint(sketch, "E58.9.8.0", {"position": v(200, 180) * mm});
            skPoint(sketch, "E58.9.9.0", {"position": v(200, 200) * mm});
            skPoint(sketch, "E58.9.10.0", {"position": v(200, 220) * mm});
            skPoint(sketch, "E58.9.11.0", {"position": v(200, 240) * mm});
            skPoint(sketch, "E58.9.12.0", {"position": v(200, 260) * mm});
            skPoint(sketch, "E58.9.13.0", {"position": v(200, 280) * mm});
            skPoint(sketch, "E58.10.0.0", {"position": v(220, 20) * mm});
            skPoint(sketch, "E58.10.1.0", {"position": v(220, 40) * mm});
            skPoint(sketch, "E58.10.2.0", {"position": v(220, 60) * mm});
            skPoint(sketch, "E58.10.3.0", {"position": v(220, 80) * mm});
            skPoint(sketch, "E58.10.4.0", {"position": v(220, 100) * mm});
            skPoint(sketch, "E58.10.5.0", {"position": v(220, 120) * mm});
            skPoint(sketch, "E58.10.6.0", {"position": v(220, 140) * mm});
            skPoint(sketch, "E58.10.7.0", {"position": v(220, 160) * mm});
            skPoint(sketch, "E58.10.8.0", {"position": v(220, 180) * mm});
            skPoint(sketch, "E58.10.9.0", {"position": v(220, 200) * mm});
            skPoint(sketch, "E58.10.10.0", {"position": v(220, 220) * mm});
            skPoint(sketch, "E58.10.11.0", {"position": v(220, 240) * mm});
            skPoint(sketch, "E58.10.12.0", {"position": v(220, 260) * mm});
            skPoint(sketch, "E58.10.13.0", {"position": v(220, 280) * mm});
            skPoint(sketch, "E58.11.0.0", {"position": v(240, 20) * mm});
            skPoint(sketch, "E58.11.1.0", {"position": v(240, 40) * mm});
            skPoint(sketch, "E58.11.2.0", {"position": v(240, 60) * mm});
            skPoint(sketch, "E58.11.3.0", {"position": v(240, 80) * mm});
            skPoint(sketch, "E58.11.4.0", {"position": v(240, 100) * mm});
            skPoint(sketch, "E58.11.5.0", {"position": v(240, 120) * mm});
            skPoint(sketch, "E58.11.6.0", {"position": v(240, 140) * mm});
            skPoint(sketch, "E58.11.7.0", {"position": v(240, 160) * mm});
            skPoint(sketch, "E58.11.8.0", {"position": v(240, 180) * mm});
            skPoint(sketch, "E58.11.9.0", {"position": v(240, 200) * mm});
            skPoint(sketch, "E58.11.10.0", {"position": v(240, 220) * mm});
            skPoint(sketch, "E58.11.11.0", {"position": v(240, 240) * mm});
            skPoint(sketch, "E58.11.12.0", {"position": v(240, 260) * mm});
            skPoint(sketch, "E58.11.13.0", {"position": v(240, 280) * mm});
            skPoint(sketch, "E58.12.0.0", {"position": v(260, 20) * mm});
            skPoint(sketch, "E58.12.1.0", {"position": v(260, 40) * mm});
            skPoint(sketch, "E58.12.2.0", {"position": v(260, 60) * mm});
            skPoint(sketch, "E58.12.3.0", {"position": v(260, 80) * mm});
            skPoint(sketch, "E58.12.4.0", {"position": v(260, 100) * mm});
            skPoint(sketch, "E58.12.5.0", {"position": v(260, 120) * mm});
            skPoint(sketch, "E58.12.6.0", {"position": v(260, 140) * mm});
            skPoint(sketch, "E58.12.7.0", {"position": v(260, 160) * mm});
            skPoint(sketch, "E58.12.8.0", {"position": v(260, 180) * mm});
            skPoint(sketch, "E58.12.9.0", {"position": v(260, 200) * mm});
            skPoint(sketch, "E58.12.10.0", {"position": v(260, 220) * mm});
            skPoint(sketch, "E58.12.11.0", {"position": v(260, 240) * mm});
            skPoint(sketch, "E58.12.12.0", {"position": v(260, 260) * mm});
            skPoint(sketch, "E58.12.13.0", {"position": v(260, 280) * mm});
            skPoint(sketch, "E58.13.0.0", {"position": v(280, 20) * mm});
            skPoint(sketch, "E58.13.1.0", {"position": v(280, 40) * mm});
            skPoint(sketch, "E58.13.2.0", {"position": v(280, 60) * mm});
            skPoint(sketch, "E58.13.3.0", {"position": v(280, 80) * mm});
            skPoint(sketch, "E58.13.4.0", {"position": v(280, 100) * mm});
            skPoint(sketch, "E58.13.5.0", {"position": v(280, 120) * mm});
            skPoint(sketch, "E58.13.6.0", {"position": v(280, 140) * mm});
            skPoint(sketch, "E58.13.7.0", {"position": v(280, 160) * mm});
            skPoint(sketch, "E58.13.8.0", {"position": v(280, 180) * mm});
            skPoint(sketch, "E58.13.9.0", {"position": v(280, 200) * mm});
            skPoint(sketch, "E58.13.10.0", {"position": v(280, 220) * mm});
            skPoint(sketch, "E58.13.11.0", {"position": v(280, 240) * mm});
            skPoint(sketch, "E58.13.12.0", {"position": v(280, 260) * mm});
            skPoint(sketch, "E58.13.13.0", {"position": v(280, 280) * mm});
            skLineSegment(sketch, "E58.direction1", {"start": v(20, 20) * mm, "end": v(40, 20) * mm, "construction": true});
            skLineSegment(sketch, "E58.direction2", {"start": v(20, 20) * mm, "end": v(20, 40) * mm, "construction": true});
            skPoint(sketch, "E59.0.0.14", {"position": v(20, 300) * mm});
            skPoint(sketch, "E59.0.1.14", {"position": v(40, 300) * mm});
            skPoint(sketch, "E59.0.2.14", {"position": v(60, 300) * mm});
            skPoint(sketch, "E59.0.3.14", {"position": v(80, 300) * mm});
            skPoint(sketch, "E59.0.4.14", {"position": v(100, 300) * mm});
            skPoint(sketch, "E59.0.5.14", {"position": v(120, 300) * mm});
            skPoint(sketch, "E59.0.6.14", {"position": v(140, 300) * mm});
            skPoint(sketch, "E59.0.7.14", {"position": v(160, 300) * mm});
            skPoint(sketch, "E59.0.8.14", {"position": v(180, 300) * mm});
            skPoint(sketch, "E59.0.9.14", {"position": v(200, 300) * mm});
            skPoint(sketch, "E59.0.10.14", {"position": v(220, 300) * mm});
            skPoint(sketch, "E59.0.11.14", {"position": v(240, 300) * mm});
            skPoint(sketch, "E59.0.12.14", {"position": v(260, 300) * mm});
            skPoint(sketch, "E59.0.13.14", {"position": v(280, 300) * mm});
            skPoint(sketch, "E60.0.14.0", {"position": v(300, 20) * mm});
            skPoint(sketch, "E60.0.14.1", {"position": v(300, 40) * mm});
            skPoint(sketch, "E60.0.14.2", {"position": v(300, 60) * mm});
            skPoint(sketch, "E60.0.14.3", {"position": v(300, 80) * mm});
            skPoint(sketch, "E60.0.14.4", {"position": v(300, 100) * mm});
            skPoint(sketch, "E60.0.14.5", {"position": v(300, 120) * mm});
            skPoint(sketch, "E60.0.14.6", {"position": v(300, 140) * mm});
            skPoint(sketch, "E60.0.14.7", {"position": v(300, 160) * mm});
            skPoint(sketch, "E60.0.14.8", {"position": v(300, 180) * mm});
            skPoint(sketch, "E60.0.14.9", {"position": v(300, 200) * mm});
            skPoint(sketch, "E60.0.14.10", {"position": v(300, 220) * mm});
            skPoint(sketch, "E60.0.14.11", {"position": v(300, 240) * mm});
            skPoint(sketch, "E60.0.14.12", {"position": v(300, 260) * mm});
            skPoint(sketch, "E60.0.14.13", {"position": v(300, 280) * mm});
            skPoint(sketch, "E60.0.14.14", {"position": v(300, 300) * mm});
            skLineSegment(sketch, "E61", {"start": v(40, 100) * mm, "end": v(40, 80) * mm});
            skLineSegment(sketch, "E62", {"start": v(40, 80) * mm, "end": v(60, 80) * mm});
            skLineSegment(sketch, "E63", {"start": v(60, 80) * mm, "end": v(60, 100) * mm});
            skLineSegment(sketch, "E64", {"start": v(60, 100) * mm, "end": v(40, 100) * mm});
            skLineSegment(sketch, "E65", {"start": v(80, 180) * mm, "end": v(80, 140) * mm});
            skLineSegment(sketch, "E66", {"start": v(80, 180) * mm, "end": v(60, 180) * mm});
            skLineSegment(sketch, "E67", {"start": v(60, 180) * mm, "end": v(60, 140) * mm});
            skLineSegment(sketch, "E68", {"start": v(80, 140) * mm, "end": v(60, 140) * mm});
            skLineSegment(sketch, "E69.bottom", {"start": v(60, 240) * mm, "end": v(40, 240) * mm});
            skLineSegment(sketch, "E69.top", {"start": v(60, 280) * mm, "end": v(40, 280) * mm});
            skLineSegment(sketch, "E69.left", {"start": v(60, 240) * mm, "end": v(60, 280) * mm});
            skLineSegment(sketch, "E69.right", {"start": v(40, 240) * mm, "end": v(40, 280) * mm});
            skLineSegment(sketch, "E70", {"start": v(100, 140) * mm, "end": v(120, 140) * mm});
            skLineSegment(sketch, "E71", {"start": v(120, 140) * mm, "end": v(120, 160) * mm});
            skLineSegment(sketch, "E72", {"start": v(140, 160) * mm, "end": v(120, 160) * mm});
            skLineSegment(sketch, "E73", {"start": v(100, 140) * mm, "end": v(100, 100) * mm});
            skLineSegment(sketch, "E74", {"start": v(140, 160) * mm, "end": v(140, 60) * mm});
            skLineSegment(sketch, "E75", {"start": v(100, 100) * mm, "end": v(120, 100) * mm});
            skLineSegment(sketch, "E76", {"start": v(120, 100) * mm, "end": v(120, 60) * mm});
            skLineSegment(sketch, "E77", {"start": v(140, 60) * mm, "end": v(120, 60) * mm});
            skLineSegment(sketch, "E78.bottom", {"start": v(160, 60) * mm, "end": v(180, 60) * mm});
            skLineSegment(sketch, "E78.top", {"start": v(160, 20) * mm, "end": v(180, 20) * mm});
            skLineSegment(sketch, "E78.left", {"start": v(160, 60) * mm, "end": v(160, 20) * mm});
            skLineSegment(sketch, "E78.right", {"start": v(180, 60) * mm, "end": v(180, 20) * mm});
            skLineSegment(sketch, "E79.bottom", {"start": v(200, 80) * mm, "end": v(220, 80) * mm});
            skLineSegment(sketch, "E79.top", {"start": v(200, 100) * mm, "end": v(220, 100) * mm});
            skLineSegment(sketch, "E79.left", {"start": v(200, 80) * mm, "end": v(200, 100) * mm});
            skLineSegment(sketch, "E79.right", {"start": v(220, 80) * mm, "end": v(220, 100) * mm});
            skLineSegment(sketch, "E80", {"start": v(180, 160) * mm, "end": v(160, 160) * mm});
            skLineSegment(sketch, "E81", {"start": v(180, 160) * mm, "end": v(180, 140) * mm});
            skLineSegment(sketch, "E82", {"start": v(180, 140) * mm, "end": v(200, 140) * mm});
            skLineSegment(sketch, "E83", {"start": v(160, 160) * mm, "end": v(160, 200) * mm});
            skLineSegment(sketch, "E84", {"start": v(160, 200) * mm, "end": v(180, 200) * mm});
            skLineSegment(sketch, "E85", {"start": v(200, 140) * mm, "end": v(200, 220) * mm});
            skLineSegment(sketch, "E86", {"start": v(200, 220) * mm, "end": v(180, 220) * mm});
            skLineSegment(sketch, "E87", {"start": v(180, 220) * mm, "end": v(180, 200) * mm});
            skLineSegment(sketch, "E88.bottom", {"start": v(140, 200) * mm, "end": v(100, 200) * mm});
            skLineSegment(sketch, "E88.top", {"start": v(140, 240) * mm, "end": v(100, 240) * mm});
            skLineSegment(sketch, "E88.left", {"start": v(140, 200) * mm, "end": v(140, 240) * mm});
            skLineSegment(sketch, "E88.right", {"start": v(100, 200) * mm, "end": v(100, 240) * mm});
            skLineSegment(sketch, "E89.bottom", {"start": v(260, 280) * mm, "end": v(240, 280) * mm});
            skLineSegment(sketch, "E89.top", {"start": v(260, 160) * mm, "end": v(240, 160) * mm});
            skLineSegment(sketch, "E89.left", {"start": v(260, 280) * mm, "end": v(260, 220) * mm});
            skLineSegment(sketch, "E89.right", {"start": v(240, 280) * mm, "end": v(240, 260) * mm});
            skLineSegment(sketch, "E90.bottom", {"start": v(240, 260) * mm, "end": v(220, 260) * mm});
            skLineSegment(sketch, "E90.top", {"start": v(240, 220) * mm, "end": v(220, 220) * mm});
            skLineSegment(sketch, "E91.bottom", {"start": v(260, 220) * mm, "end": v(280, 220) * mm});
            skLineSegment(sketch, "E91.top", {"start": v(260, 180) * mm, "end": v(280, 180) * mm});
            skLineSegment(sketch, "E92.trimOffspring", {"start": v(240, 220) * mm, "end": v(240, 160) * mm});
            skLineSegment(sketch, "E93.trimOffspring", {"start": v(260, 180) * mm, "end": v(260, 160) * mm});
            skLineSegment(sketch, "E94", {"start": v(280, 220) * mm, "end": v(280, 180) * mm});
            skLineSegment(sketch, "E95", {"start": v(220, 260) * mm, "end": v(220, 220) * mm});
            skSolve(sketch);
        }
        {
            var Q0;
            Q0 = qSketchRegion(id + "F11", true);
            extrude(context, id + "F12", {"entities" : qUnion([Q0]), "operationType" : NewBodyOperationType.REMOVE, "endBound" : BoundingType.THROUGH_ALL, "oppositeDirection" : true, "depth" : 25 * mm});
        }
        {
            var Q0;
            Q0=makeQuery(id+"F2.opPattern","COPY",FACE,{"derivedFrom":makeQuery(id+"F1.opExtrude","CAP_FACE",FACE,{"disambiguationData":[OSD([sQuery(id+"F0.wireOp",EDGE,"E0.bottom"),sQuery(id+"F0.wireOp",EDGE,"E0.top"),sQuery(id+"F0.wireOp",EDGE,"E0.left"),sQuery(id+"F0.wireOp",EDGE,"E0.right"),sQuery(id+"F0.wireOp",EDGE,"E1.top"),sQuery(id+"F0.wireOp",EDGE,"E1.left"),sQuery(id+"F0.wireOp",EDGE,"E1.right"),sQuery(id+"F0.wireOp",EDGE,"E2.bottom"),sQuery(id+"F0.wireOp",EDGE,"E2.top"),sQuery(id+"F0.wireOp",EDGE,"E2.right"),sQuery(id+"F0.wireOp",EDGE,"E3.0.1.0"),sQuery(id+"F0.wireOp",EDGE,"E3.0.1.1"),sQuery(id+"F0.wireOp",EDGE,"E3.0.1.2"),sQuery(id+"F0.wireOp",EDGE,"E3.0.2.0"),sQuery(id+"F0.wireOp",EDGE,"E3.0.2.1"),sQuery(id+"F0.wireOp",EDGE,"E3.0.2.2"),sQuery(id+"F0.wireOp",EDGE,"E3.0.3.1"),sQuery(id+"F0.wireOp",EDGE,"E3.0.3.2"),sQuery(id+"F0.wireOp",EDGE,"E4.trimOffspring"),sQuery(id+"F0.wireOp",EDGE,"E5.trimOffspring"),sQuery(id+"F0.wireOp",EDGE,"E6.trimOffspring"),sQuery(id+"F0.wireOp",EDGE,"E7.1.0.0"),sQuery(id+"F0.wireOp",EDGE,"E7.1.0.1"),sQuery(id+"F0.wireOp",EDGE,"E7.1.0.2"),sQuery(id+"F0.wireOp",EDGE,"E7.1.0.3"),sQuery(id+"F0.wireOp",EDGE,"E7.2.0.0"),sQuery(id+"F0.wireOp",EDGE,"E7.2.0.1"),sQuery(id+"F0.wireOp",EDGE,"E7.2.0.2"),sQuery(id+"F0.wireOp",EDGE,"E7.2.0.3"),sQuery(id+"F0.wireOp",EDGE,"E7.3.0.0"),sQuery(id+"F0.wireOp",EDGE,"E7.3.0.1"),sQuery(id+"F0.wireOp",EDGE,"E7.3.0.2"),sQuery(id+"F0.wireOp",EDGE,"E8.bottom"),sQuery(id+"F0.wireOp",EDGE,"E8.top"),sQuery(id+"F0.wireOp",EDGE,"E8.right"),sQuery(id+"F0.wireOp",EDGE,"E9.0.1.0"),sQuery(id+"F0.wireOp",EDGE,"E9.0.1.1"),sQuery(id+"F0.wireOp",EDGE,"E9.0.1.2"),sQuery(id+"F0.wireOp",EDGE,"E9.0.2.0"),sQuery(id+"F0.wireOp",EDGE,"E9.0.2.1"),sQuery(id+"F0.wireOp",EDGE,"E9.0.2.2"),sQuery(id+"F0.wireOp",EDGE,"E9.0.3.1"),sQuery(id+"F0.wireOp",EDGE,"E9.0.3.2"),sQuery(id+"F0.wireOp",EDGE,"E10.trimOffspring"),sQuery(id+"F0.wireOp",EDGE,"E11.trimOffspring"),sQuery(id+"F0.wireOp",EDGE,"E12.trimOffspring")])],"isStart":false}),"instanceName":"1"});
            var sketch = newSketch(context, id + "F13", { "sketchPlane" : qUnion([Q0])});
            skPoint(sketch, "E96", {"position": v(20, -40) * mm});
            skPoint(sketch, "E97.0.1.0", {"position": v(40, -40) * mm});
            skPoint(sketch, "E97.0.2.0", {"position": v(60, -40) * mm});
            skPoint(sketch, "E97.0.3.0", {"position": v(80, -40) * mm});
            skPoint(sketch, "E97.0.4.0", {"position": v(100, -40) * mm});
            skPoint(sketch, "E97.0.5.0", {"position": v(120, -40) * mm});
            skPoint(sketch, "E97.0.6.0", {"position": v(140, -40) * mm});
            skPoint(sketch, "E97.0.7.0", {"position": v(160, -40) * mm});
            skPoint(sketch, "E97.0.8.0", {"position": v(180, -40) * mm});
            skPoint(sketch, "E97.0.9.0", {"position": v(200, -40) * mm});
            skPoint(sketch, "E97.0.10.0", {"position": v(220, -40) * mm});
            skPoint(sketch, "E97.0.11.0", {"position": v(240, -40) * mm});
            skPoint(sketch, "E97.0.12.0", {"position": v(260, -40) * mm});
            skPoint(sketch, "E97.0.13.0", {"position": v(280, -40) * mm});
            skPoint(sketch, "E97.1.0.0", {"position": v(20, -60) * mm});
            skPoint(sketch, "E97.1.1.0", {"position": v(40, -60) * mm});
            skPoint(sketch, "E97.1.2.0", {"position": v(60, -60) * mm});
            skPoint(sketch, "E97.1.3.0", {"position": v(80, -60) * mm});
            skPoint(sketch, "E97.1.4.0", {"position": v(100, -60) * mm});
            skPoint(sketch, "E97.1.5.0", {"position": v(120, -60) * mm});
            skPoint(sketch, "E97.1.6.0", {"position": v(140, -60) * mm});
            skPoint(sketch, "E97.1.7.0", {"position": v(160, -60) * mm});
            skPoint(sketch, "E97.1.8.0", {"position": v(180, -60) * mm});
            skPoint(sketch, "E97.1.9.0", {"position": v(200, -60) * mm});
            skPoint(sketch, "E97.1.10.0", {"position": v(220, -60) * mm});
            skPoint(sketch, "E97.1.11.0", {"position": v(240, -60) * mm});
            skPoint(sketch, "E97.1.12.0", {"position": v(260, -60) * mm});
            skPoint(sketch, "E97.1.13.0", {"position": v(280, -60) * mm});
            skPoint(sketch, "E97.2.0.0", {"position": v(20, -80) * mm});
            skPoint(sketch, "E97.2.1.0", {"position": v(40, -80) * mm});
            skPoint(sketch, "E97.2.2.0", {"position": v(60, -80) * mm});
            skPoint(sketch, "E97.2.3.0", {"position": v(80, -80) * mm});
            skPoint(sketch, "E97.2.4.0", {"position": v(100, -80) * mm});
            skPoint(sketch, "E97.2.5.0", {"position": v(120, -80) * mm});
            skPoint(sketch, "E97.2.6.0", {"position": v(140, -80) * mm});
            skPoint(sketch, "E97.2.7.0", {"position": v(160, -80) * mm});
            skPoint(sketch, "E97.2.8.0", {"position": v(180, -80) * mm});
            skPoint(sketch, "E97.2.9.0", {"position": v(200, -80) * mm});
            skPoint(sketch, "E97.2.10.0", {"position": v(220, -80) * mm});
            skPoint(sketch, "E97.2.11.0", {"position": v(240, -80) * mm});
            skPoint(sketch, "E97.2.12.0", {"position": v(260, -80) * mm});
            skPoint(sketch, "E97.2.13.0", {"position": v(280, -80) * mm});
            skPoint(sketch, "E97.3.0.0", {"position": v(20, -100) * mm});
            skPoint(sketch, "E97.3.1.0", {"position": v(40, -100) * mm});
            skPoint(sketch, "E97.3.2.0", {"position": v(60, -100) * mm});
            skPoint(sketch, "E97.3.3.0", {"position": v(80, -100) * mm});
            skPoint(sketch, "E97.3.4.0", {"position": v(100, -100) * mm});
            skPoint(sketch, "E97.3.5.0", {"position": v(120, -100) * mm});
            skPoint(sketch, "E97.3.6.0", {"position": v(140, -100) * mm});
            skPoint(sketch, "E97.3.7.0", {"position": v(160, -100) * mm});
            skPoint(sketch, "E97.3.8.0", {"position": v(180, -100) * mm});
            skPoint(sketch, "E97.3.9.0", {"position": v(200, -100) * mm});
            skPoint(sketch, "E97.3.10.0", {"position": v(220, -100) * mm});
            skPoint(sketch, "E97.3.11.0", {"position": v(240, -100) * mm});
            skPoint(sketch, "E97.3.12.0", {"position": v(260, -100) * mm});
            skPoint(sketch, "E97.3.13.0", {"position": v(280, -100) * mm});
            skPoint(sketch, "E97.4.0.0", {"position": v(20, -120) * mm});
            skPoint(sketch, "E97.4.1.0", {"position": v(40, -120) * mm});
            skPoint(sketch, "E97.4.2.0", {"position": v(60, -120) * mm});
            skPoint(sketch, "E97.4.3.0", {"position": v(80, -120) * mm});
            skPoint(sketch, "E97.4.4.0", {"position": v(100, -120) * mm});
            skPoint(sketch, "E97.4.5.0", {"position": v(120, -120) * mm});
            skPoint(sketch, "E97.4.6.0", {"position": v(140, -120) * mm});
            skPoint(sketch, "E97.4.7.0", {"position": v(160, -120) * mm});
            skPoint(sketch, "E97.4.8.0", {"position": v(180, -120) * mm});
            skPoint(sketch, "E97.4.9.0", {"position": v(200, -120) * mm});
            skPoint(sketch, "E97.4.10.0", {"position": v(220, -120) * mm});
            skPoint(sketch, "E97.4.11.0", {"position": v(240, -120) * mm});
            skPoint(sketch, "E97.4.12.0", {"position": v(260, -120) * mm});
            skPoint(sketch, "E97.4.13.0", {"position": v(280, -120) * mm});
            skPoint(sketch, "E97.5.0.0", {"position": v(20, -140) * mm});
            skPoint(sketch, "E97.5.1.0", {"position": v(40, -140) * mm});
            skPoint(sketch, "E97.5.2.0", {"position": v(60, -140) * mm});
            skPoint(sketch, "E97.5.3.0", {"position": v(80, -140) * mm});
            skPoint(sketch, "E97.5.4.0", {"position": v(100, -140) * mm});
            skPoint(sketch, "E97.5.5.0", {"position": v(120, -140) * mm});
            skPoint(sketch, "E97.5.6.0", {"position": v(140, -140) * mm});
            skPoint(sketch, "E97.5.7.0", {"position": v(160, -140) * mm});
            skPoint(sketch, "E97.5.8.0", {"position": v(180, -140) * mm});
            skPoint(sketch, "E97.5.9.0", {"position": v(200, -140) * mm});
            skPoint(sketch, "E97.5.10.0", {"position": v(220, -140) * mm});
            skPoint(sketch, "E97.5.11.0", {"position": v(240, -140) * mm});
            skPoint(sketch, "E97.5.12.0", {"position": v(260, -140) * mm});
            skPoint(sketch, "E97.5.13.0", {"position": v(280, -140) * mm});
            skPoint(sketch, "E97.6.0.0", {"position": v(20, -160) * mm});
            skPoint(sketch, "E97.6.1.0", {"position": v(40, -160) * mm});
            skPoint(sketch, "E97.6.2.0", {"position": v(60, -160) * mm});
            skPoint(sketch, "E97.6.3.0", {"position": v(80, -160) * mm});
            skPoint(sketch, "E97.6.4.0", {"position": v(100, -160) * mm});
            skPoint(sketch, "E97.6.5.0", {"position": v(120, -160) * mm});
            skPoint(sketch, "E97.6.6.0", {"position": v(140, -160) * mm});
            skPoint(sketch, "E97.6.7.0", {"position": v(160, -160) * mm});
            skPoint(sketch, "E97.6.8.0", {"position": v(180, -160) * mm});
            skPoint(sketch, "E97.6.9.0", {"position": v(200, -160) * mm});
            skPoint(sketch, "E97.6.10.0", {"position": v(220, -160) * mm});
            skPoint(sketch, "E97.6.11.0", {"position": v(240, -160) * mm});
            skPoint(sketch, "E97.6.12.0", {"position": v(260, -160) * mm});
            skPoint(sketch, "E97.6.13.0", {"position": v(280, -160) * mm});
            skPoint(sketch, "E97.7.0.0", {"position": v(20, -180) * mm});
            skPoint(sketch, "E97.7.1.0", {"position": v(40, -180) * mm});
            skPoint(sketch, "E97.7.2.0", {"position": v(60, -180) * mm});
            skPoint(sketch, "E97.7.3.0", {"position": v(80, -180) * mm});
            skPoint(sketch, "E97.7.4.0", {"position": v(100, -180) * mm});
            skPoint(sketch, "E97.7.5.0", {"position": v(120, -180) * mm});
            skPoint(sketch, "E97.7.6.0", {"position": v(140, -180) * mm});
            skPoint(sketch, "E97.7.7.0", {"position": v(160, -180) * mm});
            skPoint(sketch, "E97.7.8.0", {"position": v(180, -180) * mm});
            skPoint(sketch, "E97.7.9.0", {"position": v(200, -180) * mm});
            skPoint(sketch, "E97.7.10.0", {"position": v(220, -180) * mm});
            skPoint(sketch, "E97.7.11.0", {"position": v(240, -180) * mm});
            skPoint(sketch, "E97.7.12.0", {"position": v(260, -180) * mm});
            skPoint(sketch, "E97.7.13.0", {"position": v(280, -180) * mm});
            skPoint(sketch, "E97.8.0.0", {"position": v(20, -200) * mm});
            skPoint(sketch, "E97.8.1.0", {"position": v(40, -200) * mm});
            skPoint(sketch, "E97.8.2.0", {"position": v(60, -200) * mm});
            skPoint(sketch, "E97.8.3.0", {"position": v(80, -200) * mm});
            skPoint(sketch, "E97.8.4.0", {"position": v(100, -200) * mm});
            skPoint(sketch, "E97.8.5.0", {"position": v(120, -200) * mm});
            skPoint(sketch, "E97.8.6.0", {"position": v(140, -200) * mm});
            skPoint(sketch, "E97.8.7.0", {"position": v(160, -200) * mm});
            skPoint(sketch, "E97.8.8.0", {"position": v(180, -200) * mm});
            skPoint(sketch, "E97.8.9.0", {"position": v(200, -200) * mm});
            skPoint(sketch, "E97.8.10.0", {"position": v(220, -200) * mm});
            skPoint(sketch, "E97.8.11.0", {"position": v(240, -200) * mm});
            skPoint(sketch, "E97.8.12.0", {"position": v(260, -200) * mm});
            skPoint(sketch, "E97.8.13.0", {"position": v(280, -200) * mm});
            skPoint(sketch, "E97.9.0.0", {"position": v(20, -220) * mm});
            skPoint(sketch, "E97.9.1.0", {"position": v(40, -220) * mm});
            skPoint(sketch, "E97.9.2.0", {"position": v(60, -220) * mm});
            skPoint(sketch, "E97.9.3.0", {"position": v(80, -220) * mm});
            skPoint(sketch, "E97.9.4.0", {"position": v(100, -220) * mm});
            skPoint(sketch, "E97.9.5.0", {"position": v(120, -220) * mm});
            skPoint(sketch, "E97.9.6.0", {"position": v(140, -220) * mm});
            skPoint(sketch, "E97.9.7.0", {"position": v(160, -220) * mm});
            skPoint(sketch, "E97.9.8.0", {"position": v(180, -220) * mm});
            skPoint(sketch, "E97.9.9.0", {"position": v(200, -220) * mm});
            skPoint(sketch, "E97.9.10.0", {"position": v(220, -220) * mm});
            skPoint(sketch, "E97.9.11.0", {"position": v(240, -220) * mm});
            skPoint(sketch, "E97.9.12.0", {"position": v(260, -220) * mm});
            skPoint(sketch, "E97.9.13.0", {"position": v(280, -220) * mm});
            skPoint(sketch, "E97.10.0.0", {"position": v(20, -240) * mm});
            skPoint(sketch, "E97.10.1.0", {"position": v(40, -240) * mm});
            skPoint(sketch, "E97.10.2.0", {"position": v(60, -240) * mm});
            skPoint(sketch, "E97.10.3.0", {"position": v(80, -240) * mm});
            skPoint(sketch, "E97.10.4.0", {"position": v(100, -240) * mm});
            skPoint(sketch, "E97.10.5.0", {"position": v(120, -240) * mm});
            skPoint(sketch, "E97.10.6.0", {"position": v(140, -240) * mm});
            skPoint(sketch, "E97.10.7.0", {"position": v(160, -240) * mm});
            skPoint(sketch, "E97.10.8.0", {"position": v(180, -240) * mm});
            skPoint(sketch, "E97.10.9.0", {"position": v(200, -240) * mm});
            skPoint(sketch, "E97.10.10.0", {"position": v(220, -240) * mm});
            skPoint(sketch, "E97.10.11.0", {"position": v(240, -240) * mm});
            skPoint(sketch, "E97.10.12.0", {"position": v(260, -240) * mm});
            skPoint(sketch, "E97.10.13.0", {"position": v(280, -240) * mm});
            skPoint(sketch, "E97.11.0.0", {"position": v(20, -260) * mm});
            skPoint(sketch, "E97.11.1.0", {"position": v(40, -260) * mm});
            skPoint(sketch, "E97.11.2.0", {"position": v(60, -260) * mm});
            skPoint(sketch, "E97.11.3.0", {"position": v(80, -260) * mm});
            skPoint(sketch, "E97.11.4.0", {"position": v(100, -260) * mm});
            skPoint(sketch, "E97.11.5.0", {"position": v(120, -260) * mm});
            skPoint(sketch, "E97.11.6.0", {"position": v(140, -260) * mm});
            skPoint(sketch, "E97.11.7.0", {"position": v(160, -260) * mm});
            skPoint(sketch, "E97.11.8.0", {"position": v(180, -260) * mm});
            skPoint(sketch, "E97.11.9.0", {"position": v(200, -260) * mm});
            skPoint(sketch, "E97.11.10.0", {"position": v(220, -260) * mm});
            skPoint(sketch, "E97.11.11.0", {"position": v(240, -260) * mm});
            skPoint(sketch, "E97.11.12.0", {"position": v(260, -260) * mm});
            skPoint(sketch, "E97.11.13.0", {"position": v(280, -260) * mm});
            skPoint(sketch, "E97.12.0.0", {"position": v(20, -280) * mm});
            skPoint(sketch, "E97.12.1.0", {"position": v(40, -280) * mm});
            skPoint(sketch, "E97.12.2.0", {"position": v(60, -280) * mm});
            skPoint(sketch, "E97.12.3.0", {"position": v(80, -280) * mm});
            skPoint(sketch, "E97.12.4.0", {"position": v(100, -280) * mm});
            skPoint(sketch, "E97.12.5.0", {"position": v(120, -280) * mm});
            skPoint(sketch, "E97.12.6.0", {"position": v(140, -280) * mm});
            skPoint(sketch, "E97.12.7.0", {"position": v(160, -280) * mm});
            skPoint(sketch, "E97.12.8.0", {"position": v(180, -280) * mm});
            skPoint(sketch, "E97.12.9.0", {"position": v(200, -280) * mm});
            skPoint(sketch, "E97.12.10.0", {"position": v(220, -280) * mm});
            skPoint(sketch, "E97.12.11.0", {"position": v(240, -280) * mm});
            skPoint(sketch, "E97.12.12.0", {"position": v(260, -280) * mm});
            skPoint(sketch, "E97.12.13.0", {"position": v(280, -280) * mm});
            skPoint(sketch, "E97.13.0.0", {"position": v(20, -300) * mm});
            skPoint(sketch, "E97.13.1.0", {"position": v(40, -300) * mm});
            skPoint(sketch, "E97.13.2.0", {"position": v(60, -300) * mm});
            skPoint(sketch, "E97.13.3.0", {"position": v(80, -300) * mm});
            skPoint(sketch, "E97.13.4.0", {"position": v(100, -300) * mm});
            skPoint(sketch, "E97.13.5.0", {"position": v(120, -300) * mm});
            skPoint(sketch, "E97.13.6.0", {"position": v(140, -300) * mm});
            skPoint(sketch, "E97.13.7.0", {"position": v(160, -300) * mm});
            skPoint(sketch, "E97.13.8.0", {"position": v(180, -300) * mm});
            skPoint(sketch, "E97.13.9.0", {"position": v(200, -300) * mm});
            skPoint(sketch, "E97.13.10.0", {"position": v(220, -300) * mm});
            skPoint(sketch, "E97.13.11.0", {"position": v(240, -300) * mm});
            skPoint(sketch, "E97.13.12.0", {"position": v(260, -300) * mm});
            skPoint(sketch, "E97.13.13.0", {"position": v(280, -300) * mm});
            skLineSegment(sketch, "E97.direction1", {"start": v(20, -40) * mm, "end": v(20, -60) * mm, "construction": true});
            skLineSegment(sketch, "E97.direction2", {"start": v(20, -40) * mm, "end": v(40, -40) * mm, "construction": true});
            skPoint(sketch, "E98.0.0.14", {"position": v(300, -40) * mm});
            skPoint(sketch, "E98.0.1.14", {"position": v(300, -60) * mm});
            skPoint(sketch, "E98.0.2.14", {"position": v(300, -80) * mm});
            skPoint(sketch, "E98.0.3.14", {"position": v(300, -100) * mm});
            skPoint(sketch, "E98.0.4.14", {"position": v(300, -120) * mm});
            skPoint(sketch, "E98.0.5.14", {"position": v(300, -140) * mm});
            skPoint(sketch, "E98.0.6.14", {"position": v(300, -160) * mm});
            skPoint(sketch, "E98.0.7.14", {"position": v(300, -180) * mm});
            skPoint(sketch, "E98.0.8.14", {"position": v(300, -200) * mm});
            skPoint(sketch, "E98.0.9.14", {"position": v(300, -220) * mm});
            skPoint(sketch, "E98.0.10.14", {"position": v(300, -240) * mm});
            skPoint(sketch, "E98.0.11.14", {"position": v(300, -260) * mm});
            skPoint(sketch, "E98.0.12.14", {"position": v(300, -280) * mm});
            skPoint(sketch, "E98.0.13.14", {"position": v(300, -300) * mm});
            skPoint(sketch, "E99.0.14.0", {"position": v(20, -320) * mm});
            skPoint(sketch, "E99.0.14.1", {"position": v(40, -320) * mm});
            skPoint(sketch, "E99.0.14.2", {"position": v(60, -320) * mm});
            skPoint(sketch, "E99.0.14.3", {"position": v(80, -320) * mm});
            skPoint(sketch, "E99.0.14.4", {"position": v(100, -320) * mm});
            skPoint(sketch, "E99.0.14.5", {"position": v(120, -320) * mm});
            skPoint(sketch, "E99.0.14.6", {"position": v(140, -320) * mm});
            skPoint(sketch, "E99.0.14.7", {"position": v(160, -320) * mm});
            skPoint(sketch, "E99.0.14.8", {"position": v(180, -320) * mm});
            skPoint(sketch, "E99.0.14.9", {"position": v(200, -320) * mm});
            skPoint(sketch, "E99.0.14.10", {"position": v(220, -320) * mm});
            skPoint(sketch, "E99.0.14.11", {"position": v(240, -320) * mm});
            skPoint(sketch, "E99.0.14.12", {"position": v(260, -320) * mm});
            skPoint(sketch, "E99.0.14.13", {"position": v(280, -320) * mm});
            skPoint(sketch, "E99.0.14.14", {"position": v(300, -320) * mm});
            skLineSegment(sketch, "E100", {"start": v(100, -60) * mm, "end": v(80, -60) * mm});
            skLineSegment(sketch, "E101", {"start": v(80, -60) * mm, "end": v(80, -80) * mm});
            skLineSegment(sketch, "E102", {"start": v(80, -80) * mm, "end": v(100, -80) * mm});
            skLineSegment(sketch, "E103", {"start": v(100, -60) * mm, "end": v(100, -80) * mm});
            skLineSegment(sketch, "E104", {"start": v(180, -100) * mm, "end": v(140, -100) * mm});
            skLineSegment(sketch, "E105", {"start": v(180, -100) * mm, "end": v(180, -80) * mm});
            skLineSegment(sketch, "E106", {"start": v(180, -80) * mm, "end": v(140, -80) * mm});
            skLineSegment(sketch, "E107", {"start": v(140, -80) * mm, "end": v(140, -100) * mm});
            skLineSegment(sketch, "E108.bottom", {"start": v(240, -80) * mm, "end": v(240, -60) * mm});
            skLineSegment(sketch, "E108.top", {"start": v(280, -80) * mm, "end": v(280, -60) * mm});
            skLineSegment(sketch, "E108.left", {"start": v(240, -80) * mm, "end": v(280, -80) * mm});
            skLineSegment(sketch, "E108.right", {"start": v(240, -60) * mm, "end": v(280, -60) * mm});
            skLineSegment(sketch, "E109", {"start": v(140, -120) * mm, "end": v(140, -140) * mm});
            skLineSegment(sketch, "E110", {"start": v(140, -140) * mm, "end": v(160, -140) * mm});
            skLineSegment(sketch, "E111", {"start": v(160, -140) * mm, "end": v(160, -160) * mm});
            skLineSegment(sketch, "E112", {"start": v(140, -120) * mm, "end": v(100, -120) * mm});
            skLineSegment(sketch, "E113", {"start": v(160, -160) * mm, "end": v(60, -160) * mm});
            skLineSegment(sketch, "E114", {"start": v(100, -120) * mm, "end": v(100, -140) * mm});
            skLineSegment(sketch, "E115", {"start": v(100, -140) * mm, "end": v(60, -140) * mm});
            skLineSegment(sketch, "E116", {"start": v(60, -140) * mm, "end": v(60, -160) * mm});
            skLineSegment(sketch, "E117.bottom", {"start": v(60, -180) * mm, "end": v(60, -200) * mm});
            skLineSegment(sketch, "E117.top", {"start": v(20, -180) * mm, "end": v(20, -200) * mm});
            skLineSegment(sketch, "E117.left", {"start": v(60, -180) * mm, "end": v(20, -180) * mm});
            skLineSegment(sketch, "E117.right", {"start": v(60, -200) * mm, "end": v(20, -200) * mm});
            skLineSegment(sketch, "E118.bottom", {"start": v(80, -220) * mm, "end": v(80, -240) * mm});
            skLineSegment(sketch, "E118.top", {"start": v(100, -220) * mm, "end": v(100, -240) * mm});
            skLineSegment(sketch, "E118.left", {"start": v(80, -220) * mm, "end": v(100, -220) * mm});
            skLineSegment(sketch, "E118.right", {"start": v(80, -240) * mm, "end": v(100, -240) * mm});
            skLineSegment(sketch, "E119", {"start": v(160, -180) * mm, "end": v(160, -200) * mm});
            skLineSegment(sketch, "E120", {"start": v(160, -200) * mm, "end": v(140, -200) * mm});
            skLineSegment(sketch, "E121", {"start": v(140, -200) * mm, "end": v(140, -220) * mm});
            skLineSegment(sketch, "E122", {"start": v(160, -180) * mm, "end": v(200, -180) * mm});
            skLineSegment(sketch, "E123", {"start": v(200, -180) * mm, "end": v(200, -200) * mm});
            skLineSegment(sketch, "E124", {"start": v(140, -220) * mm, "end": v(220, -220) * mm});
            skLineSegment(sketch, "E125", {"start": v(220, -220) * mm, "end": v(220, -200) * mm});
            skLineSegment(sketch, "E126", {"start": v(220, -200) * mm, "end": v(200, -200) * mm});
            skLineSegment(sketch, "E127.bottom", {"start": v(200, -160) * mm, "end": v(200, -120) * mm});
            skLineSegment(sketch, "E127.top", {"start": v(240, -160) * mm, "end": v(240, -120) * mm});
            skLineSegment(sketch, "E127.left", {"start": v(200, -160) * mm, "end": v(240, -160) * mm});
            skLineSegment(sketch, "E127.right", {"start": v(200, -120) * mm, "end": v(240, -120) * mm});
            skLineSegment(sketch, "E128.bottom", {"start": v(280, -280) * mm, "end": v(280, -260) * mm});
            skLineSegment(sketch, "E128.top", {"start": v(160, -280) * mm, "end": v(160, -260) * mm});
            skLineSegment(sketch, "E128.left", {"start": v(280, -280) * mm, "end": v(220, -280) * mm});
            skLineSegment(sketch, "E128.right", {"start": v(280, -260) * mm, "end": v(260, -260) * mm});
            skLineSegment(sketch, "E129.bottom", {"start": v(260, -260) * mm, "end": v(260, -240) * mm});
            skLineSegment(sketch, "E129.top", {"start": v(220, -260) * mm, "end": v(220, -240) * mm});
            skLineSegment(sketch, "E130.bottom", {"start": v(220, -280) * mm, "end": v(220, -300) * mm});
            skLineSegment(sketch, "E130.top", {"start": v(180, -280) * mm, "end": v(180, -300) * mm});
            skLineSegment(sketch, "E131.trimOffspring", {"start": v(220, -260) * mm, "end": v(160, -260) * mm});
            skLineSegment(sketch, "E132.trimOffspring", {"start": v(180, -280) * mm, "end": v(160, -280) * mm});
            skLineSegment(sketch, "E133", {"start": v(220, -300) * mm, "end": v(180, -300) * mm});
            skLineSegment(sketch, "E134", {"start": v(260, -240) * mm, "end": v(220, -240) * mm});
            skSolve(sketch);
        }
        {
            var Q0;
            Q0 = qSketchRegion(id + "F13", true);
            extrude(context, id + "F14", {"entities" : qUnion([Q0]), "operationType" : NewBodyOperationType.REMOVE, "endBound" : BoundingType.THROUGH_ALL, "oppositeDirection" : true, "depth" : 25 * mm});
        }
        {
            var Q0;
            Q0=qCreatedBy(makeId("Top.planeOp"),FACE);
            var sketch = newSketch(context, id + "F15", { "sketchPlane" : qUnion([Q0])});
            skLineSegment(sketch, "E135.bottom", {"start": v(353.73, 320) * mm, "end": v(673.73, 320) * mm});
            skLineSegment(sketch, "E135.left", {"start": v(353.73, 320) * mm, "end": v(353.73, 280) * mm});
            skLineSegment(sketch, "E135.right", {"start": v(673.73, 320) * mm, "end": v(673.73, 0) * mm});
            skLineSegment(sketch, "E136.top", {"start": v(353.73, 40) * mm, "end": v(359.73, 40) * mm});
            skLineSegment(sketch, "E136.right", {"start": v(359.73, 6) * mm, "end": v(359.73, 40) * mm});
            skLineSegment(sketch, "E137.0.1.0", {"start": v(359.73, 80) * mm, "end": v(359.73, 120) * mm});
            skLineSegment(sketch, "E137.0.1.1", {"start": v(353.73, 120) * mm, "end": v(359.73, 120) * mm});
            skLineSegment(sketch, "E137.0.1.2", {"start": v(353.73, 80) * mm, "end": v(359.73, 80) * mm});
            skLineSegment(sketch, "E137.0.2.0", {"start": v(359.73, 160) * mm, "end": v(359.73, 200) * mm});
            skLineSegment(sketch, "E137.0.2.1", {"start": v(353.73, 200) * mm, "end": v(359.73, 200) * mm});
            skLineSegment(sketch, "E137.0.2.2", {"start": v(353.73, 160) * mm, "end": v(359.73, 160) * mm});
            skLineSegment(sketch, "E137.0.3.0", {"start": v(359.73, 240) * mm, "end": v(359.73, 280) * mm});
            skLineSegment(sketch, "E137.0.3.1", {"start": v(353.73, 280) * mm, "end": v(359.73, 280) * mm});
            skLineSegment(sketch, "E137.0.3.2", {"start": v(353.73, 240) * mm, "end": v(359.73, 240) * mm});
            skLineSegment(sketch, "E137.direction1", {"start": v(345.35, 0) * mm, "end": v(358.82, 0) * mm, "construction": true});
            skLineSegment(sketch, "E137.direction2", {"start": v(359.73, 6) * mm, "end": v(359.73, 80) * mm, "construction": true});
            skLineSegment(sketch, "E138.trimOffspring", {"start": v(353.73, 80) * mm, "end": v(353.73, 40) * mm});
            skLineSegment(sketch, "E139.trimOffspring", {"start": v(353.73, 160) * mm, "end": v(353.73, 120) * mm});
            skLineSegment(sketch, "E140.trimOffspring", {"start": v(353.73, 240) * mm, "end": v(353.73, 200) * mm});
            skLineSegment(sketch, "E141.top", {"start": v(359.73, 6) * mm, "end": v(393.73, 6) * mm});
            skLineSegment(sketch, "E141.right", {"start": v(393.73, 0) * mm, "end": v(393.73, 6) * mm});
            skLineSegment(sketch, "E142.1.0.0", {"start": v(473.73, 0) * mm, "end": v(473.73, 6) * mm});
            skLineSegment(sketch, "E142.1.0.1", {"start": v(433.73, 6) * mm, "end": v(473.73, 6) * mm});
            skLineSegment(sketch, "E142.1.0.2", {"start": v(433.73, 0) * mm, "end": v(433.73, 6) * mm});
            skLineSegment(sketch, "E142.2.0.0", {"start": v(553.73, 0) * mm, "end": v(553.73, 6) * mm});
            skLineSegment(sketch, "E142.2.0.1", {"start": v(513.73, 6) * mm, "end": v(553.73, 6) * mm});
            skLineSegment(sketch, "E142.2.0.2", {"start": v(513.73, 0) * mm, "end": v(513.73, 6) * mm});
            skLineSegment(sketch, "E142.3.0.0", {"start": v(633.73, 0) * mm, "end": v(633.73, 6) * mm});
            skLineSegment(sketch, "E142.3.0.1", {"start": v(593.73, 6) * mm, "end": v(633.73, 6) * mm});
            skLineSegment(sketch, "E142.3.0.2", {"start": v(593.73, 0) * mm, "end": v(593.73, 6) * mm});
            skLineSegment(sketch, "E142.direction1", {"start": v(393.73, 0) * mm, "end": v(433.73, 0) * mm, "construction": true});
            skLineSegment(sketch, "E143.trimOffspring", {"start": v(553.73, 0) * mm, "end": v(593.73, 0) * mm});
            skLineSegment(sketch, "E144.trimOffspring", {"start": v(633.73, 0) * mm, "end": v(673.73, 0) * mm});
            skLineSegment(sketch, "E145.trimOffspring", {"start": v(393.73, 0) * mm, "end": v(433.73, 0) * mm});
            skLineSegment(sketch, "E146.trimOffspring", {"start": v(473.73, 0) * mm, "end": v(513.73, 0) * mm});
            skSolve(sketch);
        }
        {
            var Q0;
            Q0=makeQuery(id+"F15.imprint","IMPRINT",FACE,{"disambiguationData":[TD([[makeQuery(id+"F15.imprint","IMPRINT",EDGE,{"derivedFrom":sQuery(id+"F15.wireOp",EDGE,"E135.bottom")}),-1.0]])]});
            extrude(context, id + "F16", {"entities" : qUnion([Q0]), "depth" : 6 * mm});
        }
        {
            var Q0;
            Q0=makeQuery(id+"F16.opExtrude","SWEPT_BODY",BODY,{"disambiguationData":[OSD([sQuery(id+"F15.wireOp",EDGE,"E135.bottom"),sQuery(id+"F15.wireOp",EDGE,"E135.left"),sQuery(id+"F15.wireOp",EDGE,"E135.right"),sQuery(id+"F15.wireOp",EDGE,"E136.top"),sQuery(id+"F15.wireOp",EDGE,"E136.right"),sQuery(id+"F15.wireOp",EDGE,"E137.0.1.0"),sQuery(id+"F15.wireOp",EDGE,"E137.0.1.1"),sQuery(id+"F15.wireOp",EDGE,"E137.0.1.2"),sQuery(id+"F15.wireOp",EDGE,"E137.0.2.0"),sQuery(id+"F15.wireOp",EDGE,"E137.0.2.1"),sQuery(id+"F15.wireOp",EDGE,"E137.0.2.2"),sQuery(id+"F15.wireOp",EDGE,"E137.0.3.0"),sQuery(id+"F15.wireOp",EDGE,"E137.0.3.1"),sQuery(id+"F15.wireOp",EDGE,"E137.0.3.2"),sQuery(id+"F15.wireOp",EDGE,"E138.trimOffspring"),sQuery(id+"F15.wireOp",EDGE,"E139.trimOffspring"),sQuery(id+"F15.wireOp",EDGE,"E140.trimOffspring"),sQuery(id+"F15.wireOp",EDGE,"E141.top"),sQuery(id+"F15.wireOp",EDGE,"E141.right"),sQuery(id+"F15.wireOp",EDGE,"E142.1.0.0"),sQuery(id+"F15.wireOp",EDGE,"E142.1.0.1"),sQuery(id+"F15.wireOp",EDGE,"E142.1.0.2"),sQuery(id+"F15.wireOp",EDGE,"E142.2.0.0"),sQuery(id+"F15.wireOp",EDGE,"E142.2.0.1"),sQuery(id+"F15.wireOp",EDGE,"E142.2.0.2"),sQuery(id+"F15.wireOp",EDGE,"E142.3.0.0"),sQuery(id+"F15.wireOp",EDGE,"E142.3.0.1"),sQuery(id+"F15.wireOp",EDGE,"E142.3.0.2"),sQuery(id+"F15.wireOp",EDGE,"E143.trimOffspring"),sQuery(id+"F15.wireOp",EDGE,"E144.trimOffspring"),sQuery(id+"F15.wireOp",EDGE,"E145.trimOffspring"),sQuery(id+"F15.wireOp",EDGE,"E146.trimOffspring")])]});
            var Q1;
            Q1=qCreatedBy(makeId("Right.planeOp"),FACE);
            mirror(context, id + "F17", {"entities" : qUnion([Q0]), "mirrorPlane" : qUnion([Q1])});
        }
        {
            var Q0;
            Q0=makeQuery(id+"F17.opPattern","COPY",BODY,{"derivedFrom":makeQuery(id+"F16.opExtrude","SWEPT_BODY",BODY,{"disambiguationData":[OSD([sQuery(id+"F15.wireOp",EDGE,"E135.bottom"),sQuery(id+"F15.wireOp",EDGE,"E135.left"),sQuery(id+"F15.wireOp",EDGE,"E135.right"),sQuery(id+"F15.wireOp",EDGE,"E136.top"),sQuery(id+"F15.wireOp",EDGE,"E136.right"),sQuery(id+"F15.wireOp",EDGE,"E137.0.1.0"),sQuery(id+"F15.wireOp",EDGE,"E137.0.1.1"),sQuery(id+"F15.wireOp",EDGE,"E137.0.1.2"),sQuery(id+"F15.wireOp",EDGE,"E137.0.2.0"),sQuery(id+"F15.wireOp",EDGE,"E137.0.2.1"),sQuery(id+"F15.wireOp",EDGE,"E137.0.2.2"),sQuery(id+"F15.wireOp",EDGE,"E137.0.3.0"),sQuery(id+"F15.wireOp",EDGE,"E137.0.3.1"),sQuery(id+"F15.wireOp",EDGE,"E137.0.3.2"),sQuery(id+"F15.wireOp",EDGE,"E138.trimOffspring"),sQuery(id+"F15.wireOp",EDGE,"E139.trimOffspring"),sQuery(id+"F15.wireOp",EDGE,"E140.trimOffspring"),sQuery(id+"F15.wireOp",EDGE,"E141.top"),sQuery(id+"F15.wireOp",EDGE,"E141.right"),sQuery(id+"F15.wireOp",EDGE,"E142.1.0.0"),sQuery(id+"F15.wireOp",EDGE,"E142.1.0.1"),sQuery(id+"F15.wireOp",EDGE,"E142.1.0.2"),sQuery(id+"F15.wireOp",EDGE,"E142.2.0.0"),sQuery(id+"F15.wireOp",EDGE,"E142.2.0.1"),sQuery(id+"F15.wireOp",EDGE,"E142.2.0.2"),sQuery(id+"F15.wireOp",EDGE,"E142.3.0.0"),sQuery(id+"F15.wireOp",EDGE,"E142.3.0.1"),sQuery(id+"F15.wireOp",EDGE,"E142.3.0.2"),sQuery(id+"F15.wireOp",EDGE,"E143.trimOffspring"),sQuery(id+"F15.wireOp",EDGE,"E144.trimOffspring"),sQuery(id+"F15.wireOp",EDGE,"E145.trimOffspring"),sQuery(id+"F15.wireOp",EDGE,"E146.trimOffspring")])]}),"instanceName":"1"});
            transform(context, id + "F18", {"entities" : qUnion([Q0]), "transformType" : TransformType.TRANSLATION_3D, "dx" : 318 * mm, "dy" : 0 * mm, "dz" : 0 * mm, "makeCopy" : false});
        }
        {
            var Q0;
            Q0=makeQuery(id+"F16.opExtrude","CAP_FACE",FACE,{"disambiguationData":[OSD([sQuery(id+"F15.wireOp",EDGE,"E135.bottom"),sQuery(id+"F15.wireOp",EDGE,"E135.left"),sQuery(id+"F15.wireOp",EDGE,"E135.right"),sQuery(id+"F15.wireOp",EDGE,"E136.top"),sQuery(id+"F15.wireOp",EDGE,"E136.right"),sQuery(id+"F15.wireOp",EDGE,"E137.0.1.0"),sQuery(id+"F15.wireOp",EDGE,"E137.0.1.1"),sQuery(id+"F15.wireOp",EDGE,"E137.0.1.2"),sQuery(id+"F15.wireOp",EDGE,"E137.0.2.0"),sQuery(id+"F15.wireOp",EDGE,"E137.0.2.1"),sQuery(id+"F15.wireOp",EDGE,"E137.0.2.2"),sQuery(id+"F15.wireOp",EDGE,"E137.0.3.0"),sQuery(id+"F15.wireOp",EDGE,"E137.0.3.1"),sQuery(id+"F15.wireOp",EDGE,"E137.0.3.2"),sQuery(id+"F15.wireOp",EDGE,"E138.trimOffspring"),sQuery(id+"F15.wireOp",EDGE,"E139.trimOffspring"),sQuery(id+"F15.wireOp",EDGE,"E140.trimOffspring"),sQuery(id+"F15.wireOp",EDGE,"E141.top"),sQuery(id+"F15.wireOp",EDGE,"E141.right"),sQuery(id+"F15.wireOp",EDGE,"E142.1.0.0"),sQuery(id+"F15.wireOp",EDGE,"E142.1.0.1"),sQuery(id+"F15.wireOp",EDGE,"E142.1.0.2"),sQuery(id+"F15.wireOp",EDGE,"E142.2.0.0"),sQuery(id+"F15.wireOp",EDGE,"E142.2.0.1"),sQuery(id+"F15.wireOp",EDGE,"E142.2.0.2"),sQuery(id+"F15.wireOp",EDGE,"E142.3.0.0"),sQuery(id+"F15.wireOp",EDGE,"E142.3.0.1"),sQuery(id+"F15.wireOp",EDGE,"E142.3.0.2"),sQuery(id+"F15.wireOp",EDGE,"E143.trimOffspring"),sQuery(id+"F15.wireOp",EDGE,"E144.trimOffspring"),sQuery(id+"F15.wireOp",EDGE,"E145.trimOffspring"),sQuery(id+"F15.wireOp",EDGE,"E146.trimOffspring")])],"isStart":false});
            var sketch = newSketch(context, id + "F19", { "sketchPlane" : qUnion([Q0])});
            skPoint(sketch, "E147", {"position": v(373.73, 20) * mm});
            skPoint(sketch, "E148.0.1.0", {"position": v(373.73, 40) * mm});
            skPoint(sketch, "E148.0.2.0", {"position": v(373.73, 60) * mm});
            skPoint(sketch, "E148.0.3.0", {"position": v(373.73, 80) * mm});
            skPoint(sketch, "E148.0.4.0", {"position": v(373.73, 100) * mm});
            skPoint(sketch, "E148.0.5.0", {"position": v(373.73, 120) * mm});
            skPoint(sketch, "E148.0.6.0", {"position": v(373.73, 140) * mm});
            skPoint(sketch, "E148.0.7.0", {"position": v(373.73, 160) * mm});
            skPoint(sketch, "E148.0.8.0", {"position": v(373.73, 180) * mm});
            skPoint(sketch, "E148.0.9.0", {"position": v(373.73, 200) * mm});
            skPoint(sketch, "E148.0.10.0", {"position": v(373.73, 220) * mm});
            skPoint(sketch, "E148.0.11.0", {"position": v(373.73, 240) * mm});
            skPoint(sketch, "E148.0.12.0", {"position": v(373.73, 260) * mm});
            skPoint(sketch, "E148.0.13.0", {"position": v(373.73, 280) * mm});
            skPoint(sketch, "E148.1.0.0", {"position": v(393.73, 20) * mm});
            skPoint(sketch, "E148.1.1.0", {"position": v(393.73, 40) * mm});
            skPoint(sketch, "E148.1.2.0", {"position": v(393.73, 60) * mm});
            skPoint(sketch, "E148.1.3.0", {"position": v(393.73, 80) * mm});
            skPoint(sketch, "E148.1.4.0", {"position": v(393.73, 100) * mm});
            skPoint(sketch, "E148.1.5.0", {"position": v(393.73, 120) * mm});
            skPoint(sketch, "E148.1.6.0", {"position": v(393.73, 140) * mm});
            skPoint(sketch, "E148.1.7.0", {"position": v(393.73, 160) * mm});
            skPoint(sketch, "E148.1.8.0", {"position": v(393.73, 180) * mm});
            skPoint(sketch, "E148.1.9.0", {"position": v(393.73, 200) * mm});
            skPoint(sketch, "E148.1.10.0", {"position": v(393.73, 220) * mm});
            skPoint(sketch, "E148.1.11.0", {"position": v(393.73, 240) * mm});
            skPoint(sketch, "E148.1.12.0", {"position": v(393.73, 260) * mm});
            skPoint(sketch, "E148.1.13.0", {"position": v(393.73, 280) * mm});
            skPoint(sketch, "E148.2.0.0", {"position": v(413.73, 20) * mm});
            skPoint(sketch, "E148.2.1.0", {"position": v(413.73, 40) * mm});
            skPoint(sketch, "E148.2.2.0", {"position": v(413.73, 60) * mm});
            skPoint(sketch, "E148.2.3.0", {"position": v(413.73, 80) * mm});
            skPoint(sketch, "E148.2.4.0", {"position": v(413.73, 100) * mm});
            skPoint(sketch, "E148.2.5.0", {"position": v(413.73, 120) * mm});
            skPoint(sketch, "E148.2.6.0", {"position": v(413.73, 140) * mm});
            skPoint(sketch, "E148.2.7.0", {"position": v(413.73, 160) * mm});
            skPoint(sketch, "E148.2.8.0", {"position": v(413.73, 180) * mm});
            skPoint(sketch, "E148.2.9.0", {"position": v(413.73, 200) * mm});
            skPoint(sketch, "E148.2.10.0", {"position": v(413.73, 220) * mm});
            skPoint(sketch, "E148.2.11.0", {"position": v(413.73, 240) * mm});
            skPoint(sketch, "E148.2.12.0", {"position": v(413.73, 260) * mm});
            skPoint(sketch, "E148.2.13.0", {"position": v(413.73, 280) * mm});
            skPoint(sketch, "E148.3.0.0", {"position": v(433.73, 20) * mm});
            skPoint(sketch, "E148.3.1.0", {"position": v(433.73, 40) * mm});
            skPoint(sketch, "E148.3.2.0", {"position": v(433.73, 60) * mm});
            skPoint(sketch, "E148.3.3.0", {"position": v(433.73, 80) * mm});
            skPoint(sketch, "E148.3.4.0", {"position": v(433.73, 100) * mm});
            skPoint(sketch, "E148.3.5.0", {"position": v(433.73, 120) * mm});
            skPoint(sketch, "E148.3.6.0", {"position": v(433.73, 140) * mm});
            skPoint(sketch, "E148.3.7.0", {"position": v(433.73, 160) * mm});
            skPoint(sketch, "E148.3.8.0", {"position": v(433.73, 180) * mm});
            skPoint(sketch, "E148.3.9.0", {"position": v(433.73, 200) * mm});
            skPoint(sketch, "E148.3.10.0", {"position": v(433.73, 220) * mm});
            skPoint(sketch, "E148.3.11.0", {"position": v(433.73, 240) * mm});
            skPoint(sketch, "E148.3.12.0", {"position": v(433.73, 260) * mm});
            skPoint(sketch, "E148.3.13.0", {"position": v(433.73, 280) * mm});
            skPoint(sketch, "E148.4.0.0", {"position": v(453.73, 20) * mm});
            skPoint(sketch, "E148.4.1.0", {"position": v(453.73, 40) * mm});
            skPoint(sketch, "E148.4.2.0", {"position": v(453.73, 60) * mm});
            skPoint(sketch, "E148.4.3.0", {"position": v(453.73, 80) * mm});
            skPoint(sketch, "E148.4.4.0", {"position": v(453.73, 100) * mm});
            skPoint(sketch, "E148.4.5.0", {"position": v(453.73, 120) * mm});
            skPoint(sketch, "E148.4.6.0", {"position": v(453.73, 140) * mm});
            skPoint(sketch, "E148.4.7.0", {"position": v(453.73, 160) * mm});
            skPoint(sketch, "E148.4.8.0", {"position": v(453.73, 180) * mm});
            skPoint(sketch, "E148.4.9.0", {"position": v(453.73, 200) * mm});
            skPoint(sketch, "E148.4.10.0", {"position": v(453.73, 220) * mm});
            skPoint(sketch, "E148.4.11.0", {"position": v(453.73, 240) * mm});
            skPoint(sketch, "E148.4.12.0", {"position": v(453.73, 260) * mm});
            skPoint(sketch, "E148.4.13.0", {"position": v(453.73, 280) * mm});
            skPoint(sketch, "E148.5.0.0", {"position": v(473.73, 20) * mm});
            skPoint(sketch, "E148.5.1.0", {"position": v(473.73, 40) * mm});
            skPoint(sketch, "E148.5.2.0", {"position": v(473.73, 60) * mm});
            skPoint(sketch, "E148.5.3.0", {"position": v(473.73, 80) * mm});
            skPoint(sketch, "E148.5.4.0", {"position": v(473.73, 100) * mm});
            skPoint(sketch, "E148.5.5.0", {"position": v(473.73, 120) * mm});
            skPoint(sketch, "E148.5.6.0", {"position": v(473.73, 140) * mm});
            skPoint(sketch, "E148.5.7.0", {"position": v(473.73, 160) * mm});
            skPoint(sketch, "E148.5.8.0", {"position": v(473.73, 180) * mm});
            skPoint(sketch, "E148.5.9.0", {"position": v(473.73, 200) * mm});
            skPoint(sketch, "E148.5.10.0", {"position": v(473.73, 220) * mm});
            skPoint(sketch, "E148.5.11.0", {"position": v(473.73, 240) * mm});
            skPoint(sketch, "E148.5.12.0", {"position": v(473.73, 260) * mm});
            skPoint(sketch, "E148.5.13.0", {"position": v(473.73, 280) * mm});
            skPoint(sketch, "E148.6.0.0", {"position": v(493.73, 20) * mm});
            skPoint(sketch, "E148.6.1.0", {"position": v(493.73, 40) * mm});
            skPoint(sketch, "E148.6.2.0", {"position": v(493.73, 60) * mm});
            skPoint(sketch, "E148.6.3.0", {"position": v(493.73, 80) * mm});
            skPoint(sketch, "E148.6.4.0", {"position": v(493.73, 100) * mm});
            skPoint(sketch, "E148.6.5.0", {"position": v(493.73, 120) * mm});
            skPoint(sketch, "E148.6.6.0", {"position": v(493.73, 140) * mm});
            skPoint(sketch, "E148.6.7.0", {"position": v(493.73, 160) * mm});
            skPoint(sketch, "E148.6.8.0", {"position": v(493.73, 180) * mm});
            skPoint(sketch, "E148.6.9.0", {"position": v(493.73, 200) * mm});
            skPoint(sketch, "E148.6.10.0", {"position": v(493.73, 220) * mm});
            skPoint(sketch, "E148.6.11.0", {"position": v(493.73, 240) * mm});
            skPoint(sketch, "E148.6.12.0", {"position": v(493.73, 260) * mm});
            skPoint(sketch, "E148.6.13.0", {"position": v(493.73, 280) * mm});
            skPoint(sketch, "E148.7.0.0", {"position": v(513.73, 20) * mm});
            skPoint(sketch, "E148.7.1.0", {"position": v(513.73, 40) * mm});
            skPoint(sketch, "E148.7.2.0", {"position": v(513.73, 60) * mm});
            skPoint(sketch, "E148.7.3.0", {"position": v(513.73, 80) * mm});
            skPoint(sketch, "E148.7.4.0", {"position": v(513.73, 100) * mm});
            skPoint(sketch, "E148.7.5.0", {"position": v(513.73, 120) * mm});
            skPoint(sketch, "E148.7.6.0", {"position": v(513.73, 140) * mm});
            skPoint(sketch, "E148.7.7.0", {"position": v(513.73, 160) * mm});
            skPoint(sketch, "E148.7.8.0", {"position": v(513.73, 180) * mm});
            skPoint(sketch, "E148.7.9.0", {"position": v(513.73, 200) * mm});
            skPoint(sketch, "E148.7.10.0", {"position": v(513.73, 220) * mm});
            skPoint(sketch, "E148.7.11.0", {"position": v(513.73, 240) * mm});
            skPoint(sketch, "E148.7.12.0", {"position": v(513.73, 260) * mm});
            skPoint(sketch, "E148.7.13.0", {"position": v(513.73, 280) * mm});
            skPoint(sketch, "E148.8.0.0", {"position": v(533.73, 20) * mm});
            skPoint(sketch, "E148.8.1.0", {"position": v(533.73, 40) * mm});
            skPoint(sketch, "E148.8.2.0", {"position": v(533.73, 60) * mm});
            skPoint(sketch, "E148.8.3.0", {"position": v(533.73, 80) * mm});
            skPoint(sketch, "E148.8.4.0", {"position": v(533.73, 100) * mm});
            skPoint(sketch, "E148.8.5.0", {"position": v(533.73, 120) * mm});
            skPoint(sketch, "E148.8.6.0", {"position": v(533.73, 140) * mm});
            skPoint(sketch, "E148.8.7.0", {"position": v(533.73, 160) * mm});
            skPoint(sketch, "E148.8.8.0", {"position": v(533.73, 180) * mm});
            skPoint(sketch, "E148.8.9.0", {"position": v(533.73, 200) * mm});
            skPoint(sketch, "E148.8.10.0", {"position": v(533.73, 220) * mm});
            skPoint(sketch, "E148.8.11.0", {"position": v(533.73, 240) * mm});
            skPoint(sketch, "E148.8.12.0", {"position": v(533.73, 260) * mm});
            skPoint(sketch, "E148.8.13.0", {"position": v(533.73, 280) * mm});
            skPoint(sketch, "E148.9.0.0", {"position": v(553.73, 20) * mm});
            skPoint(sketch, "E148.9.1.0", {"position": v(553.73, 40) * mm});
            skPoint(sketch, "E148.9.2.0", {"position": v(553.73, 60) * mm});
            skPoint(sketch, "E148.9.3.0", {"position": v(553.73, 80) * mm});
            skPoint(sketch, "E148.9.4.0", {"position": v(553.73, 100) * mm});
            skPoint(sketch, "E148.9.5.0", {"position": v(553.73, 120) * mm});
            skPoint(sketch, "E148.9.6.0", {"position": v(553.73, 140) * mm});
            skPoint(sketch, "E148.9.7.0", {"position": v(553.73, 160) * mm});
            skPoint(sketch, "E148.9.8.0", {"position": v(553.73, 180) * mm});
            skPoint(sketch, "E148.9.9.0", {"position": v(553.73, 200) * mm});
            skPoint(sketch, "E148.9.10.0", {"position": v(553.73, 220) * mm});
            skPoint(sketch, "E148.9.11.0", {"position": v(553.73, 240) * mm});
            skPoint(sketch, "E148.9.12.0", {"position": v(553.73, 260) * mm});
            skPoint(sketch, "E148.9.13.0", {"position": v(553.73, 280) * mm});
            skPoint(sketch, "E148.10.0.0", {"position": v(573.73, 20) * mm});
            skPoint(sketch, "E148.10.1.0", {"position": v(573.73, 40) * mm});
            skPoint(sketch, "E148.10.2.0", {"position": v(573.73, 60) * mm});
            skPoint(sketch, "E148.10.3.0", {"position": v(573.73, 80) * mm});
            skPoint(sketch, "E148.10.4.0", {"position": v(573.73, 100) * mm});
            skPoint(sketch, "E148.10.5.0", {"position": v(573.73, 120) * mm});
            skPoint(sketch, "E148.10.6.0", {"position": v(573.73, 140) * mm});
            skPoint(sketch, "E148.10.7.0", {"position": v(573.73, 160) * mm});
            skPoint(sketch, "E148.10.8.0", {"position": v(573.73, 180) * mm});
            skPoint(sketch, "E148.10.9.0", {"position": v(573.73, 200) * mm});
            skPoint(sketch, "E148.10.10.0", {"position": v(573.73, 220) * mm});
            skPoint(sketch, "E148.10.11.0", {"position": v(573.73, 240) * mm});
            skPoint(sketch, "E148.10.12.0", {"position": v(573.73, 260) * mm});
            skPoint(sketch, "E148.10.13.0", {"position": v(573.73, 280) * mm});
            skPoint(sketch, "E148.11.0.0", {"position": v(593.73, 20) * mm});
            skPoint(sketch, "E148.11.1.0", {"position": v(593.73, 40) * mm});
            skPoint(sketch, "E148.11.2.0", {"position": v(593.73, 60) * mm});
            skPoint(sketch, "E148.11.3.0", {"position": v(593.73, 80) * mm});
            skPoint(sketch, "E148.11.4.0", {"position": v(593.73, 100) * mm});
            skPoint(sketch, "E148.11.5.0", {"position": v(593.73, 120) * mm});
            skPoint(sketch, "E148.11.6.0", {"position": v(593.73, 140) * mm});
            skPoint(sketch, "E148.11.7.0", {"position": v(593.73, 160) * mm});
            skPoint(sketch, "E148.11.8.0", {"position": v(593.73, 180) * mm});
            skPoint(sketch, "E148.11.9.0", {"position": v(593.73, 200) * mm});
            skPoint(sketch, "E148.11.10.0", {"position": v(593.73, 220) * mm});
            skPoint(sketch, "E148.11.11.0", {"position": v(593.73, 240) * mm});
            skPoint(sketch, "E148.11.12.0", {"position": v(593.73, 260) * mm});
            skPoint(sketch, "E148.11.13.0", {"position": v(593.73, 280) * mm});
            skPoint(sketch, "E148.12.0.0", {"position": v(613.73, 20) * mm});
            skPoint(sketch, "E148.12.1.0", {"position": v(613.73, 40) * mm});
            skPoint(sketch, "E148.12.2.0", {"position": v(613.73, 60) * mm});
            skPoint(sketch, "E148.12.3.0", {"position": v(613.73, 80) * mm});
            skPoint(sketch, "E148.12.4.0", {"position": v(613.73, 100) * mm});
            skPoint(sketch, "E148.12.5.0", {"position": v(613.73, 120) * mm});
            skPoint(sketch, "E148.12.6.0", {"position": v(613.73, 140) * mm});
            skPoint(sketch, "E148.12.7.0", {"position": v(613.73, 160) * mm});
            skPoint(sketch, "E148.12.8.0", {"position": v(613.73, 180) * mm});
            skPoint(sketch, "E148.12.9.0", {"position": v(613.73, 200) * mm});
            skPoint(sketch, "E148.12.10.0", {"position": v(613.73, 220) * mm});
            skPoint(sketch, "E148.12.11.0", {"position": v(613.73, 240) * mm});
            skPoint(sketch, "E148.12.12.0", {"position": v(613.73, 260) * mm});
            skPoint(sketch, "E148.12.13.0", {"position": v(613.73, 280) * mm});
            skPoint(sketch, "E148.13.0.0", {"position": v(633.73, 20) * mm});
            skPoint(sketch, "E148.13.1.0", {"position": v(633.73, 40) * mm});
            skPoint(sketch, "E148.13.2.0", {"position": v(633.73, 60) * mm});
            skPoint(sketch, "E148.13.3.0", {"position": v(633.73, 80) * mm});
            skPoint(sketch, "E148.13.4.0", {"position": v(633.73, 100) * mm});
            skPoint(sketch, "E148.13.5.0", {"position": v(633.73, 120) * mm});
            skPoint(sketch, "E148.13.6.0", {"position": v(633.73, 140) * mm});
            skPoint(sketch, "E148.13.7.0", {"position": v(633.73, 160) * mm});
            skPoint(sketch, "E148.13.8.0", {"position": v(633.73, 180) * mm});
            skPoint(sketch, "E148.13.9.0", {"position": v(633.73, 200) * mm});
            skPoint(sketch, "E148.13.10.0", {"position": v(633.73, 220) * mm});
            skPoint(sketch, "E148.13.11.0", {"position": v(633.73, 240) * mm});
            skPoint(sketch, "E148.13.12.0", {"position": v(633.73, 260) * mm});
            skPoint(sketch, "E148.13.13.0", {"position": v(633.73, 280) * mm});
            skLineSegment(sketch, "E148.direction1", {"start": v(373.73, 20) * mm, "end": v(393.73, 20) * mm, "construction": true});
            skLineSegment(sketch, "E148.direction2", {"start": v(373.73, 20) * mm, "end": v(373.73, 40) * mm, "construction": true});
            skPoint(sketch, "E149.0.0.14", {"position": v(373.73, 300) * mm});
            skPoint(sketch, "E149.0.1.14", {"position": v(393.73, 300) * mm});
            skPoint(sketch, "E149.0.2.14", {"position": v(413.73, 300) * mm});
            skPoint(sketch, "E149.0.3.14", {"position": v(433.73, 300) * mm});
            skPoint(sketch, "E149.0.4.14", {"position": v(453.73, 300) * mm});
            skPoint(sketch, "E149.0.5.14", {"position": v(473.73, 300) * mm});
            skPoint(sketch, "E149.0.6.14", {"position": v(493.73, 300) * mm});
            skPoint(sketch, "E149.0.7.14", {"position": v(513.73, 300) * mm});
            skPoint(sketch, "E149.0.8.14", {"position": v(533.73, 300) * mm});
            skPoint(sketch, "E149.0.9.14", {"position": v(553.73, 300) * mm});
            skPoint(sketch, "E149.0.10.14", {"position": v(573.73, 300) * mm});
            skPoint(sketch, "E149.0.11.14", {"position": v(593.73, 300) * mm});
            skPoint(sketch, "E149.0.12.14", {"position": v(613.73, 300) * mm});
            skPoint(sketch, "E149.0.13.14", {"position": v(633.73, 300) * mm});
            skPoint(sketch, "E150.0.14.0", {"position": v(653.73, 20) * mm});
            skPoint(sketch, "E150.0.14.1", {"position": v(653.73, 40) * mm});
            skPoint(sketch, "E150.0.14.2", {"position": v(653.73, 60) * mm});
            skPoint(sketch, "E150.0.14.3", {"position": v(653.73, 80) * mm});
            skPoint(sketch, "E150.0.14.4", {"position": v(653.73, 100) * mm});
            skPoint(sketch, "E150.0.14.5", {"position": v(653.73, 120) * mm});
            skPoint(sketch, "E150.0.14.6", {"position": v(653.73, 140) * mm});
            skPoint(sketch, "E150.0.14.7", {"position": v(653.73, 160) * mm});
            skPoint(sketch, "E150.0.14.8", {"position": v(653.73, 180) * mm});
            skPoint(sketch, "E150.0.14.9", {"position": v(653.73, 200) * mm});
            skPoint(sketch, "E150.0.14.10", {"position": v(653.73, 220) * mm});
            skPoint(sketch, "E150.0.14.11", {"position": v(653.73, 240) * mm});
            skPoint(sketch, "E150.0.14.12", {"position": v(653.73, 260) * mm});
            skPoint(sketch, "E150.0.14.13", {"position": v(653.73, 280) * mm});
            skPoint(sketch, "E150.0.14.14", {"position": v(653.73, 300) * mm});
            skLineSegment(sketch, "E151", {"start": v(393.73, 100) * mm, "end": v(393.73, 80) * mm});
            skLineSegment(sketch, "E152", {"start": v(393.73, 80) * mm, "end": v(413.73, 80) * mm});
            skLineSegment(sketch, "E153", {"start": v(413.73, 80) * mm, "end": v(413.73, 100) * mm});
            skLineSegment(sketch, "E154", {"start": v(413.73, 100) * mm, "end": v(393.73, 100) * mm});
            skLineSegment(sketch, "E155", {"start": v(433.73, 180) * mm, "end": v(433.73, 140) * mm});
            skLineSegment(sketch, "E156", {"start": v(433.73, 180) * mm, "end": v(413.73, 180) * mm});
            skLineSegment(sketch, "E157", {"start": v(413.73, 180) * mm, "end": v(413.73, 140) * mm});
            skLineSegment(sketch, "E158", {"start": v(433.73, 140) * mm, "end": v(413.73, 140) * mm});
            skLineSegment(sketch, "E159.bottom", {"start": v(413.73, 240) * mm, "end": v(393.73, 240) * mm});
            skLineSegment(sketch, "E159.top", {"start": v(413.73, 280) * mm, "end": v(393.73, 280) * mm});
            skLineSegment(sketch, "E159.left", {"start": v(413.73, 240) * mm, "end": v(413.73, 280) * mm});
            skLineSegment(sketch, "E159.right", {"start": v(393.73, 240) * mm, "end": v(393.73, 280) * mm});
            skLineSegment(sketch, "E160", {"start": v(453.73, 140) * mm, "end": v(473.73, 140) * mm});
            skLineSegment(sketch, "E161", {"start": v(473.73, 140) * mm, "end": v(473.73, 160) * mm});
            skLineSegment(sketch, "E162", {"start": v(493.73, 160) * mm, "end": v(473.73, 160) * mm});
            skLineSegment(sketch, "E163", {"start": v(453.73, 140) * mm, "end": v(453.73, 100) * mm});
            skLineSegment(sketch, "E164", {"start": v(493.73, 160) * mm, "end": v(493.73, 60) * mm});
            skLineSegment(sketch, "E165", {"start": v(453.73, 100) * mm, "end": v(473.73, 100) * mm});
            skLineSegment(sketch, "E166", {"start": v(473.73, 100) * mm, "end": v(473.73, 60) * mm});
            skLineSegment(sketch, "E167", {"start": v(493.73, 60) * mm, "end": v(473.73, 60) * mm});
            skLineSegment(sketch, "E168.bottom", {"start": v(513.73, 60) * mm, "end": v(533.73, 60) * mm});
            skLineSegment(sketch, "E168.top", {"start": v(513.73, 20) * mm, "end": v(533.73, 20) * mm});
            skLineSegment(sketch, "E168.left", {"start": v(513.73, 60) * mm, "end": v(513.73, 20) * mm});
            skLineSegment(sketch, "E168.right", {"start": v(533.73, 60) * mm, "end": v(533.73, 20) * mm});
            skLineSegment(sketch, "E169.bottom", {"start": v(553.73, 80) * mm, "end": v(573.73, 80) * mm});
            skLineSegment(sketch, "E169.top", {"start": v(553.73, 100) * mm, "end": v(573.73, 100) * mm});
            skLineSegment(sketch, "E169.left", {"start": v(553.73, 80) * mm, "end": v(553.73, 100) * mm});
            skLineSegment(sketch, "E169.right", {"start": v(573.73, 80) * mm, "end": v(573.73, 100) * mm});
            skLineSegment(sketch, "E170", {"start": v(533.73, 160) * mm, "end": v(513.73, 160) * mm});
            skLineSegment(sketch, "E171", {"start": v(533.73, 160) * mm, "end": v(533.73, 140) * mm});
            skLineSegment(sketch, "E172", {"start": v(533.73, 140) * mm, "end": v(553.73, 140) * mm});
            skLineSegment(sketch, "E173", {"start": v(513.73, 160) * mm, "end": v(513.73, 200) * mm});
            skLineSegment(sketch, "E174", {"start": v(513.73, 200) * mm, "end": v(533.73, 200) * mm});
            skLineSegment(sketch, "E175", {"start": v(553.73, 140) * mm, "end": v(553.73, 220) * mm});
            skLineSegment(sketch, "E176", {"start": v(553.73, 220) * mm, "end": v(533.73, 220) * mm});
            skLineSegment(sketch, "E177", {"start": v(533.73, 220) * mm, "end": v(533.73, 200) * mm});
            skLineSegment(sketch, "E178.bottom", {"start": v(493.73, 200) * mm, "end": v(453.73, 200) * mm});
            skLineSegment(sketch, "E178.top", {"start": v(493.73, 240) * mm, "end": v(453.73, 240) * mm});
            skLineSegment(sketch, "E178.left", {"start": v(493.73, 200) * mm, "end": v(493.73, 240) * mm});
            skLineSegment(sketch, "E178.right", {"start": v(453.73, 200) * mm, "end": v(453.73, 240) * mm});
            skLineSegment(sketch, "E179.bottom", {"start": v(613.73, 280) * mm, "end": v(593.73, 280) * mm});
            skLineSegment(sketch, "E179.top", {"start": v(613.73, 160) * mm, "end": v(593.73, 160) * mm});
            skLineSegment(sketch, "E179.left", {"start": v(613.73, 280) * mm, "end": v(613.73, 220) * mm});
            skLineSegment(sketch, "E179.right", {"start": v(593.73, 280) * mm, "end": v(593.73, 260) * mm});
            skLineSegment(sketch, "E180.bottom", {"start": v(593.73, 260) * mm, "end": v(573.73, 260) * mm});
            skLineSegment(sketch, "E180.top", {"start": v(593.73, 220) * mm, "end": v(573.73, 220) * mm});
            skLineSegment(sketch, "E181.bottom", {"start": v(613.73, 220) * mm, "end": v(633.73, 220) * mm});
            skLineSegment(sketch, "E181.top", {"start": v(613.73, 180) * mm, "end": v(633.73, 180) * mm});
            skLineSegment(sketch, "E182.trimOffspring", {"start": v(593.73, 220) * mm, "end": v(593.73, 160) * mm});
            skLineSegment(sketch, "E183.trimOffspring", {"start": v(613.73, 180) * mm, "end": v(613.73, 160) * mm});
            skLineSegment(sketch, "E184", {"start": v(633.73, 220) * mm, "end": v(633.73, 180) * mm});
            skLineSegment(sketch, "E185", {"start": v(573.73, 260) * mm, "end": v(573.73, 220) * mm});
            skSolve(sketch);
        }
        {
            var Q0;
            Q0 = qSketchRegion(id + "F19", true);
            extrude(context, id + "F20", {"entities" : qUnion([Q0]), "operationType" : NewBodyOperationType.REMOVE, "endBound" : BoundingType.THROUGH_ALL, "oppositeDirection" : true, "depth" : 25 * mm});
        }
        {
            var Q0;
            Q0=makeQuery(id+"F17.opPattern","COPY",FACE,{"derivedFrom":makeQuery(id+"F16.opExtrude","CAP_FACE",FACE,{"disambiguationData":[OSD([sQuery(id+"F15.wireOp",EDGE,"E135.bottom"),sQuery(id+"F15.wireOp",EDGE,"E135.left"),sQuery(id+"F15.wireOp",EDGE,"E135.right"),sQuery(id+"F15.wireOp",EDGE,"E136.top"),sQuery(id+"F15.wireOp",EDGE,"E136.right"),sQuery(id+"F15.wireOp",EDGE,"E137.0.1.0"),sQuery(id+"F15.wireOp",EDGE,"E137.0.1.1"),sQuery(id+"F15.wireOp",EDGE,"E137.0.1.2"),sQuery(id+"F15.wireOp",EDGE,"E137.0.2.0"),sQuery(id+"F15.wireOp",EDGE,"E137.0.2.1"),sQuery(id+"F15.wireOp",EDGE,"E137.0.2.2"),sQuery(id+"F15.wireOp",EDGE,"E137.0.3.0"),sQuery(id+"F15.wireOp",EDGE,"E137.0.3.1"),sQuery(id+"F15.wireOp",EDGE,"E137.0.3.2"),sQuery(id+"F15.wireOp",EDGE,"E138.trimOffspring"),sQuery(id+"F15.wireOp",EDGE,"E139.trimOffspring"),sQuery(id+"F15.wireOp",EDGE,"E140.trimOffspring"),sQuery(id+"F15.wireOp",EDGE,"E141.top"),sQuery(id+"F15.wireOp",EDGE,"E141.right"),sQuery(id+"F15.wireOp",EDGE,"E142.1.0.0"),sQuery(id+"F15.wireOp",EDGE,"E142.1.0.1"),sQuery(id+"F15.wireOp",EDGE,"E142.1.0.2"),sQuery(id+"F15.wireOp",EDGE,"E142.2.0.0"),sQuery(id+"F15.wireOp",EDGE,"E142.2.0.1"),sQuery(id+"F15.wireOp",EDGE,"E142.2.0.2"),sQuery(id+"F15.wireOp",EDGE,"E142.3.0.0"),sQuery(id+"F15.wireOp",EDGE,"E142.3.0.1"),sQuery(id+"F15.wireOp",EDGE,"E142.3.0.2"),sQuery(id+"F15.wireOp",EDGE,"E143.trimOffspring"),sQuery(id+"F15.wireOp",EDGE,"E144.trimOffspring"),sQuery(id+"F15.wireOp",EDGE,"E145.trimOffspring"),sQuery(id+"F15.wireOp",EDGE,"E146.trimOffspring")])],"isStart":false}),"instanceName":"1"});
            var sketch = newSketch(context, id + "F21", { "sketchPlane" : qUnion([Q0])});
            skPoint(sketch, "E186", {"position": v(-55.73, 300) * mm});
            skPoint(sketch, "E187.0.1.0", {"position": v(-55.73, 280) * mm});
            skPoint(sketch, "E187.0.2.0", {"position": v(-55.73, 260) * mm});
            skPoint(sketch, "E187.0.3.0", {"position": v(-55.73, 240) * mm});
            skPoint(sketch, "E187.0.4.0", {"position": v(-55.73, 220) * mm});
            skPoint(sketch, "E187.0.5.0", {"position": v(-55.73, 200) * mm});
            skPoint(sketch, "E187.0.6.0", {"position": v(-55.73, 180) * mm});
            skPoint(sketch, "E187.0.7.0", {"position": v(-55.73, 160) * mm});
            skPoint(sketch, "E187.0.8.0", {"position": v(-55.73, 140) * mm});
            skPoint(sketch, "E187.0.9.0", {"position": v(-55.73, 120) * mm});
            skPoint(sketch, "E187.0.10.0", {"position": v(-55.73, 100) * mm});
            skPoint(sketch, "E187.0.11.0", {"position": v(-55.73, 80) * mm});
            skPoint(sketch, "E187.0.12.0", {"position": v(-55.73, 60) * mm});
            skPoint(sketch, "E187.0.13.0", {"position": v(-55.73, 40) * mm});
            skPoint(sketch, "E187.1.0.0", {"position": v(-75.73, 300) * mm});
            skPoint(sketch, "E187.1.1.0", {"position": v(-75.73, 280) * mm});
            skPoint(sketch, "E187.1.2.0", {"position": v(-75.73, 260) * mm});
            skPoint(sketch, "E187.1.3.0", {"position": v(-75.73, 240) * mm});
            skPoint(sketch, "E187.1.4.0", {"position": v(-75.73, 220) * mm});
            skPoint(sketch, "E187.1.5.0", {"position": v(-75.73, 200) * mm});
            skPoint(sketch, "E187.1.6.0", {"position": v(-75.73, 180) * mm});
            skPoint(sketch, "E187.1.7.0", {"position": v(-75.73, 160) * mm});
            skPoint(sketch, "E187.1.8.0", {"position": v(-75.73, 140) * mm});
            skPoint(sketch, "E187.1.9.0", {"position": v(-75.73, 120) * mm});
            skPoint(sketch, "E187.1.10.0", {"position": v(-75.73, 100) * mm});
            skPoint(sketch, "E187.1.11.0", {"position": v(-75.73, 80) * mm});
            skPoint(sketch, "E187.1.12.0", {"position": v(-75.73, 60) * mm});
            skPoint(sketch, "E187.1.13.0", {"position": v(-75.73, 40) * mm});
            skPoint(sketch, "E187.2.0.0", {"position": v(-95.73, 300) * mm});
            skPoint(sketch, "E187.2.1.0", {"position": v(-95.73, 280) * mm});
            skPoint(sketch, "E187.2.2.0", {"position": v(-95.73, 260) * mm});
            skPoint(sketch, "E187.2.3.0", {"position": v(-95.73, 240) * mm});
            skPoint(sketch, "E187.2.4.0", {"position": v(-95.73, 220) * mm});
            skPoint(sketch, "E187.2.5.0", {"position": v(-95.73, 200) * mm});
            skPoint(sketch, "E187.2.6.0", {"position": v(-95.73, 180) * mm});
            skPoint(sketch, "E187.2.7.0", {"position": v(-95.73, 160) * mm});
            skPoint(sketch, "E187.2.8.0", {"position": v(-95.73, 140) * mm});
            skPoint(sketch, "E187.2.9.0", {"position": v(-95.73, 120) * mm});
            skPoint(sketch, "E187.2.10.0", {"position": v(-95.73, 100) * mm});
            skPoint(sketch, "E187.2.11.0", {"position": v(-95.73, 80) * mm});
            skPoint(sketch, "E187.2.12.0", {"position": v(-95.73, 60) * mm});
            skPoint(sketch, "E187.2.13.0", {"position": v(-95.73, 40) * mm});
            skPoint(sketch, "E187.3.0.0", {"position": v(-115.73, 300) * mm});
            skPoint(sketch, "E187.3.1.0", {"position": v(-115.73, 280) * mm});
            skPoint(sketch, "E187.3.2.0", {"position": v(-115.73, 260) * mm});
            skPoint(sketch, "E187.3.3.0", {"position": v(-115.73, 240) * mm});
            skPoint(sketch, "E187.3.4.0", {"position": v(-115.73, 220) * mm});
            skPoint(sketch, "E187.3.5.0", {"position": v(-115.73, 200) * mm});
            skPoint(sketch, "E187.3.6.0", {"position": v(-115.73, 180) * mm});
            skPoint(sketch, "E187.3.7.0", {"position": v(-115.73, 160) * mm});
            skPoint(sketch, "E187.3.8.0", {"position": v(-115.73, 140) * mm});
            skPoint(sketch, "E187.3.9.0", {"position": v(-115.73, 120) * mm});
            skPoint(sketch, "E187.3.10.0", {"position": v(-115.73, 100) * mm});
            skPoint(sketch, "E187.3.11.0", {"position": v(-115.73, 80) * mm});
            skPoint(sketch, "E187.3.12.0", {"position": v(-115.73, 60) * mm});
            skPoint(sketch, "E187.3.13.0", {"position": v(-115.73, 40) * mm});
            skPoint(sketch, "E187.4.0.0", {"position": v(-135.73, 300) * mm});
            skPoint(sketch, "E187.4.1.0", {"position": v(-135.73, 280) * mm});
            skPoint(sketch, "E187.4.2.0", {"position": v(-135.73, 260) * mm});
            skPoint(sketch, "E187.4.3.0", {"position": v(-135.73, 240) * mm});
            skPoint(sketch, "E187.4.4.0", {"position": v(-135.73, 220) * mm});
            skPoint(sketch, "E187.4.5.0", {"position": v(-135.73, 200) * mm});
            skPoint(sketch, "E187.4.6.0", {"position": v(-135.73, 180) * mm});
            skPoint(sketch, "E187.4.7.0", {"position": v(-135.73, 160) * mm});
            skPoint(sketch, "E187.4.8.0", {"position": v(-135.73, 140) * mm});
            skPoint(sketch, "E187.4.9.0", {"position": v(-135.73, 120) * mm});
            skPoint(sketch, "E187.4.10.0", {"position": v(-135.73, 100) * mm});
            skPoint(sketch, "E187.4.11.0", {"position": v(-135.73, 80) * mm});
            skPoint(sketch, "E187.4.12.0", {"position": v(-135.73, 60) * mm});
            skPoint(sketch, "E187.4.13.0", {"position": v(-135.73, 40) * mm});
            skPoint(sketch, "E187.5.0.0", {"position": v(-155.73, 300) * mm});
            skPoint(sketch, "E187.5.1.0", {"position": v(-155.73, 280) * mm});
            skPoint(sketch, "E187.5.2.0", {"position": v(-155.73, 260) * mm});
            skPoint(sketch, "E187.5.3.0", {"position": v(-155.73, 240) * mm});
            skPoint(sketch, "E187.5.4.0", {"position": v(-155.73, 220) * mm});
            skPoint(sketch, "E187.5.5.0", {"position": v(-155.73, 200) * mm});
            skPoint(sketch, "E187.5.6.0", {"position": v(-155.73, 180) * mm});
            skPoint(sketch, "E187.5.7.0", {"position": v(-155.73, 160) * mm});
            skPoint(sketch, "E187.5.8.0", {"position": v(-155.73, 140) * mm});
            skPoint(sketch, "E187.5.9.0", {"position": v(-155.73, 120) * mm});
            skPoint(sketch, "E187.5.10.0", {"position": v(-155.73, 100) * mm});
            skPoint(sketch, "E187.5.11.0", {"position": v(-155.73, 80) * mm});
            skPoint(sketch, "E187.5.12.0", {"position": v(-155.73, 60) * mm});
            skPoint(sketch, "E187.5.13.0", {"position": v(-155.73, 40) * mm});
            skPoint(sketch, "E187.6.0.0", {"position": v(-175.73, 300) * mm});
            skPoint(sketch, "E187.6.1.0", {"position": v(-175.73, 280) * mm});
            skPoint(sketch, "E187.6.2.0", {"position": v(-175.73, 260) * mm});
            skPoint(sketch, "E187.6.3.0", {"position": v(-175.73, 240) * mm});
            skPoint(sketch, "E187.6.4.0", {"position": v(-175.73, 220) * mm});
            skPoint(sketch, "E187.6.5.0", {"position": v(-175.73, 200) * mm});
            skPoint(sketch, "E187.6.6.0", {"position": v(-175.73, 180) * mm});
            skPoint(sketch, "E187.6.7.0", {"position": v(-175.73, 160) * mm});
            skPoint(sketch, "E187.6.8.0", {"position": v(-175.73, 140) * mm});
            skPoint(sketch, "E187.6.9.0", {"position": v(-175.73, 120) * mm});
            skPoint(sketch, "E187.6.10.0", {"position": v(-175.73, 100) * mm});
            skPoint(sketch, "E187.6.11.0", {"position": v(-175.73, 80) * mm});
            skPoint(sketch, "E187.6.12.0", {"position": v(-175.73, 60) * mm});
            skPoint(sketch, "E187.6.13.0", {"position": v(-175.73, 40) * mm});
            skPoint(sketch, "E187.7.0.0", {"position": v(-195.73, 300) * mm});
            skPoint(sketch, "E187.7.1.0", {"position": v(-195.73, 280) * mm});
            skPoint(sketch, "E187.7.2.0", {"position": v(-195.73, 260) * mm});
            skPoint(sketch, "E187.7.3.0", {"position": v(-195.73, 240) * mm});
            skPoint(sketch, "E187.7.4.0", {"position": v(-195.73, 220) * mm});
            skPoint(sketch, "E187.7.5.0", {"position": v(-195.73, 200) * mm});
            skPoint(sketch, "E187.7.6.0", {"position": v(-195.73, 180) * mm});
            skPoint(sketch, "E187.7.7.0", {"position": v(-195.73, 160) * mm});
            skPoint(sketch, "E187.7.8.0", {"position": v(-195.73, 140) * mm});
            skPoint(sketch, "E187.7.9.0", {"position": v(-195.73, 120) * mm});
            skPoint(sketch, "E187.7.10.0", {"position": v(-195.73, 100) * mm});
            skPoint(sketch, "E187.7.11.0", {"position": v(-195.73, 80) * mm});
            skPoint(sketch, "E187.7.12.0", {"position": v(-195.73, 60) * mm});
            skPoint(sketch, "E187.7.13.0", {"position": v(-195.73, 40) * mm});
            skPoint(sketch, "E187.8.0.0", {"position": v(-215.73, 300) * mm});
            skPoint(sketch, "E187.8.1.0", {"position": v(-215.73, 280) * mm});
            skPoint(sketch, "E187.8.2.0", {"position": v(-215.73, 260) * mm});
            skPoint(sketch, "E187.8.3.0", {"position": v(-215.73, 240) * mm});
            skPoint(sketch, "E187.8.4.0", {"position": v(-215.73, 220) * mm});
            skPoint(sketch, "E187.8.5.0", {"position": v(-215.73, 200) * mm});
            skPoint(sketch, "E187.8.6.0", {"position": v(-215.73, 180) * mm});
            skPoint(sketch, "E187.8.7.0", {"position": v(-215.73, 160) * mm});
            skPoint(sketch, "E187.8.8.0", {"position": v(-215.73, 140) * mm});
            skPoint(sketch, "E187.8.9.0", {"position": v(-215.73, 120) * mm});
            skPoint(sketch, "E187.8.10.0", {"position": v(-215.73, 100) * mm});
            skPoint(sketch, "E187.8.11.0", {"position": v(-215.73, 80) * mm});
            skPoint(sketch, "E187.8.12.0", {"position": v(-215.73, 60) * mm});
            skPoint(sketch, "E187.8.13.0", {"position": v(-215.73, 40) * mm});
            skPoint(sketch, "E187.9.0.0", {"position": v(-235.73, 300) * mm});
            skPoint(sketch, "E187.9.1.0", {"position": v(-235.73, 280) * mm});
            skPoint(sketch, "E187.9.2.0", {"position": v(-235.73, 260) * mm});
            skPoint(sketch, "E187.9.3.0", {"position": v(-235.73, 240) * mm});
            skPoint(sketch, "E187.9.4.0", {"position": v(-235.73, 220) * mm});
            skPoint(sketch, "E187.9.5.0", {"position": v(-235.73, 200) * mm});
            skPoint(sketch, "E187.9.6.0", {"position": v(-235.73, 180) * mm});
            skPoint(sketch, "E187.9.7.0", {"position": v(-235.73, 160) * mm});
            skPoint(sketch, "E187.9.8.0", {"position": v(-235.73, 140) * mm});
            skPoint(sketch, "E187.9.9.0", {"position": v(-235.73, 120) * mm});
            skPoint(sketch, "E187.9.10.0", {"position": v(-235.73, 100) * mm});
            skPoint(sketch, "E187.9.11.0", {"position": v(-235.73, 80) * mm});
            skPoint(sketch, "E187.9.12.0", {"position": v(-235.73, 60) * mm});
            skPoint(sketch, "E187.9.13.0", {"position": v(-235.73, 40) * mm});
            skPoint(sketch, "E187.10.0.0", {"position": v(-255.73, 300) * mm});
            skPoint(sketch, "E187.10.1.0", {"position": v(-255.73, 280) * mm});
            skPoint(sketch, "E187.10.2.0", {"position": v(-255.73, 260) * mm});
            skPoint(sketch, "E187.10.3.0", {"position": v(-255.73, 240) * mm});
            skPoint(sketch, "E187.10.4.0", {"position": v(-255.73, 220) * mm});
            skPoint(sketch, "E187.10.5.0", {"position": v(-255.73, 200) * mm});
            skPoint(sketch, "E187.10.6.0", {"position": v(-255.73, 180) * mm});
            skPoint(sketch, "E187.10.7.0", {"position": v(-255.73, 160) * mm});
            skPoint(sketch, "E187.10.8.0", {"position": v(-255.73, 140) * mm});
            skPoint(sketch, "E187.10.9.0", {"position": v(-255.73, 120) * mm});
            skPoint(sketch, "E187.10.10.0", {"position": v(-255.73, 100) * mm});
            skPoint(sketch, "E187.10.11.0", {"position": v(-255.73, 80) * mm});
            skPoint(sketch, "E187.10.12.0", {"position": v(-255.73, 60) * mm});
            skPoint(sketch, "E187.10.13.0", {"position": v(-255.73, 40) * mm});
            skPoint(sketch, "E187.11.0.0", {"position": v(-275.73, 300) * mm});
            skPoint(sketch, "E187.11.1.0", {"position": v(-275.73, 280) * mm});
            skPoint(sketch, "E187.11.2.0", {"position": v(-275.73, 260) * mm});
            skPoint(sketch, "E187.11.3.0", {"position": v(-275.73, 240) * mm});
            skPoint(sketch, "E187.11.4.0", {"position": v(-275.73, 220) * mm});
            skPoint(sketch, "E187.11.5.0", {"position": v(-275.73, 200) * mm});
            skPoint(sketch, "E187.11.6.0", {"position": v(-275.73, 180) * mm});
            skPoint(sketch, "E187.11.7.0", {"position": v(-275.73, 160) * mm});
            skPoint(sketch, "E187.11.8.0", {"position": v(-275.73, 140) * mm});
            skPoint(sketch, "E187.11.9.0", {"position": v(-275.73, 120) * mm});
            skPoint(sketch, "E187.11.10.0", {"position": v(-275.73, 100) * mm});
            skPoint(sketch, "E187.11.11.0", {"position": v(-275.73, 80) * mm});
            skPoint(sketch, "E187.11.12.0", {"position": v(-275.73, 60) * mm});
            skPoint(sketch, "E187.11.13.0", {"position": v(-275.73, 40) * mm});
            skPoint(sketch, "E187.12.0.0", {"position": v(-295.73, 300) * mm});
            skPoint(sketch, "E187.12.1.0", {"position": v(-295.73, 280) * mm});
            skPoint(sketch, "E187.12.2.0", {"position": v(-295.73, 260) * mm});
            skPoint(sketch, "E187.12.3.0", {"position": v(-295.73, 240) * mm});
            skPoint(sketch, "E187.12.4.0", {"position": v(-295.73, 220) * mm});
            skPoint(sketch, "E187.12.5.0", {"position": v(-295.73, 200) * mm});
            skPoint(sketch, "E187.12.6.0", {"position": v(-295.73, 180) * mm});
            skPoint(sketch, "E187.12.7.0", {"position": v(-295.73, 160) * mm});
            skPoint(sketch, "E187.12.8.0", {"position": v(-295.73, 140) * mm});
            skPoint(sketch, "E187.12.9.0", {"position": v(-295.73, 120) * mm});
            skPoint(sketch, "E187.12.10.0", {"position": v(-295.73, 100) * mm});
            skPoint(sketch, "E187.12.11.0", {"position": v(-295.73, 80) * mm});
            skPoint(sketch, "E187.12.12.0", {"position": v(-295.73, 60) * mm});
            skPoint(sketch, "E187.12.13.0", {"position": v(-295.73, 40) * mm});
            skPoint(sketch, "E187.13.0.0", {"position": v(-315.73, 300) * mm});
            skPoint(sketch, "E187.13.1.0", {"position": v(-315.73, 280) * mm});
            skPoint(sketch, "E187.13.2.0", {"position": v(-315.73, 260) * mm});
            skPoint(sketch, "E187.13.3.0", {"position": v(-315.73, 240) * mm});
            skPoint(sketch, "E187.13.4.0", {"position": v(-315.73, 220) * mm});
            skPoint(sketch, "E187.13.5.0", {"position": v(-315.73, 200) * mm});
            skPoint(sketch, "E187.13.6.0", {"position": v(-315.73, 180) * mm});
            skPoint(sketch, "E187.13.7.0", {"position": v(-315.73, 160) * mm});
            skPoint(sketch, "E187.13.8.0", {"position": v(-315.73, 140) * mm});
            skPoint(sketch, "E187.13.9.0", {"position": v(-315.73, 120) * mm});
            skPoint(sketch, "E187.13.10.0", {"position": v(-315.73, 100) * mm});
            skPoint(sketch, "E187.13.11.0", {"position": v(-315.73, 80) * mm});
            skPoint(sketch, "E187.13.12.0", {"position": v(-315.73, 60) * mm});
            skPoint(sketch, "E187.13.13.0", {"position": v(-315.73, 40) * mm});
            skLineSegment(sketch, "E187.direction1", {"start": v(-55.73, 300) * mm, "end": v(-75.73, 300) * mm, "construction": true});
            skLineSegment(sketch, "E187.direction2", {"start": v(-55.73, 300) * mm, "end": v(-55.73, 280) * mm, "construction": true});
            skPoint(sketch, "E188.0.0.14", {"position": v(-55.73, 20) * mm});
            skPoint(sketch, "E188.0.1.14", {"position": v(-75.73, 20) * mm});
            skPoint(sketch, "E188.0.2.14", {"position": v(-95.73, 20) * mm});
            skPoint(sketch, "E188.0.3.14", {"position": v(-115.73, 20) * mm});
            skPoint(sketch, "E188.0.4.14", {"position": v(-135.73, 20) * mm});
            skPoint(sketch, "E188.0.5.14", {"position": v(-155.73, 20) * mm});
            skPoint(sketch, "E188.0.6.14", {"position": v(-175.73, 20) * mm});
            skPoint(sketch, "E188.0.7.14", {"position": v(-195.73, 20) * mm});
            skPoint(sketch, "E188.0.8.14", {"position": v(-215.73, 20) * mm});
            skPoint(sketch, "E188.0.9.14", {"position": v(-235.73, 20) * mm});
            skPoint(sketch, "E188.0.10.14", {"position": v(-255.73, 20) * mm});
            skPoint(sketch, "E188.0.11.14", {"position": v(-275.73, 20) * mm});
            skPoint(sketch, "E188.0.12.14", {"position": v(-295.73, 20) * mm});
            skPoint(sketch, "E188.0.13.14", {"position": v(-315.73, 20) * mm});
            skPoint(sketch, "E189.0.14.0", {"position": v(-335.73, 300) * mm});
            skPoint(sketch, "E189.0.14.1", {"position": v(-335.73, 280) * mm});
            skPoint(sketch, "E189.0.14.2", {"position": v(-335.73, 260) * mm});
            skPoint(sketch, "E189.0.14.3", {"position": v(-335.73, 240) * mm});
            skPoint(sketch, "E189.0.14.4", {"position": v(-335.73, 220) * mm});
            skPoint(sketch, "E189.0.14.5", {"position": v(-335.73, 200) * mm});
            skPoint(sketch, "E189.0.14.6", {"position": v(-335.73, 180) * mm});
            skPoint(sketch, "E189.0.14.7", {"position": v(-335.73, 160) * mm});
            skPoint(sketch, "E189.0.14.8", {"position": v(-335.73, 140) * mm});
            skPoint(sketch, "E189.0.14.9", {"position": v(-335.73, 120) * mm});
            skPoint(sketch, "E189.0.14.10", {"position": v(-335.73, 100) * mm});
            skPoint(sketch, "E189.0.14.11", {"position": v(-335.73, 80) * mm});
            skPoint(sketch, "E189.0.14.12", {"position": v(-335.73, 60) * mm});
            skPoint(sketch, "E189.0.14.13", {"position": v(-335.73, 40) * mm});
            skPoint(sketch, "E189.0.14.14", {"position": v(-335.73, 20) * mm});
            skLineSegment(sketch, "E190", {"start": v(-75.73, 240) * mm, "end": v(-75.73, 220) * mm});
            skLineSegment(sketch, "E191", {"start": v(-75.73, 240) * mm, "end": v(-95.73, 240) * mm});
            skLineSegment(sketch, "E192", {"start": v(-95.73, 240) * mm, "end": v(-95.73, 220) * mm});
            skLineSegment(sketch, "E193", {"start": v(-75.73, 220) * mm, "end": v(-95.73, 220) * mm});
            skLineSegment(sketch, "E194", {"start": v(-115.73, 180) * mm, "end": v(-115.73, 140) * mm});
            skLineSegment(sketch, "E195", {"start": v(-115.73, 140) * mm, "end": v(-95.73, 140) * mm});
            skLineSegment(sketch, "E196", {"start": v(-95.73, 140) * mm, "end": v(-95.73, 180) * mm});
            skLineSegment(sketch, "E197", {"start": v(-95.73, 180) * mm, "end": v(-115.73, 180) * mm});
            skLineSegment(sketch, "E198.bottom", {"start": v(-95.73, 80) * mm, "end": v(-75.73, 80) * mm});
            skLineSegment(sketch, "E198.top", {"start": v(-95.73, 40) * mm, "end": v(-75.73, 40) * mm});
            skLineSegment(sketch, "E198.left", {"start": v(-95.73, 80) * mm, "end": v(-95.73, 40) * mm});
            skLineSegment(sketch, "E198.right", {"start": v(-75.73, 80) * mm, "end": v(-75.73, 40) * mm});
            skLineSegment(sketch, "E199", {"start": v(-135.73, 180) * mm, "end": v(-155.73, 180) * mm});
            skLineSegment(sketch, "E200", {"start": v(-155.73, 180) * mm, "end": v(-155.73, 160) * mm});
            skLineSegment(sketch, "E201", {"start": v(-155.73, 160) * mm, "end": v(-175.73, 160) * mm});
            skLineSegment(sketch, "E202", {"start": v(-135.73, 220) * mm, "end": v(-135.73, 180) * mm});
            skLineSegment(sketch, "E203", {"start": v(-175.73, 160) * mm, "end": v(-175.73, 260) * mm});
            skLineSegment(sketch, "E204", {"start": v(-135.73, 220) * mm, "end": v(-155.73, 220) * mm});
            skLineSegment(sketch, "E205", {"start": v(-155.73, 220) * mm, "end": v(-155.73, 260) * mm});
            skLineSegment(sketch, "E206", {"start": v(-155.73, 260) * mm, "end": v(-175.73, 260) * mm});
            skLineSegment(sketch, "E207.bottom", {"start": v(-195.73, 260) * mm, "end": v(-215.73, 260) * mm});
            skLineSegment(sketch, "E207.top", {"start": v(-195.73, 300) * mm, "end": v(-215.73, 300) * mm});
            skLineSegment(sketch, "E207.left", {"start": v(-195.73, 260) * mm, "end": v(-195.73, 300) * mm});
            skLineSegment(sketch, "E207.right", {"start": v(-215.73, 260) * mm, "end": v(-215.73, 300) * mm});
            skLineSegment(sketch, "E208.bottom", {"start": v(-235.73, 240) * mm, "end": v(-255.73, 240) * mm});
            skLineSegment(sketch, "E208.top", {"start": v(-235.73, 220) * mm, "end": v(-255.73, 220) * mm});
            skLineSegment(sketch, "E208.left", {"start": v(-235.73, 240) * mm, "end": v(-235.73, 220) * mm});
            skLineSegment(sketch, "E208.right", {"start": v(-255.73, 240) * mm, "end": v(-255.73, 220) * mm});
            skLineSegment(sketch, "E209", {"start": v(-195.73, 160) * mm, "end": v(-215.73, 160) * mm});
            skLineSegment(sketch, "E210", {"start": v(-215.73, 160) * mm, "end": v(-215.73, 180) * mm});
            skLineSegment(sketch, "E211", {"start": v(-215.73, 180) * mm, "end": v(-235.73, 180) * mm});
            skLineSegment(sketch, "E212", {"start": v(-195.73, 160) * mm, "end": v(-195.73, 120) * mm});
            skLineSegment(sketch, "E213", {"start": v(-195.73, 120) * mm, "end": v(-215.73, 120) * mm});
            skLineSegment(sketch, "E214", {"start": v(-235.73, 180) * mm, "end": v(-235.73, 100) * mm});
            skLineSegment(sketch, "E215", {"start": v(-235.73, 100) * mm, "end": v(-215.73, 100) * mm});
            skLineSegment(sketch, "E216", {"start": v(-215.73, 120) * mm, "end": v(-215.73, 100) * mm});
            skLineSegment(sketch, "E217.bottom", {"start": v(-175.73, 120) * mm, "end": v(-135.73, 120) * mm});
            skLineSegment(sketch, "E217.top", {"start": v(-175.73, 80) * mm, "end": v(-135.73, 80) * mm});
            skLineSegment(sketch, "E217.left", {"start": v(-175.73, 120) * mm, "end": v(-175.73, 80) * mm});
            skLineSegment(sketch, "E217.right", {"start": v(-135.73, 120) * mm, "end": v(-135.73, 80) * mm});
            skLineSegment(sketch, "E218.bottom", {"start": v(-295.73, 40) * mm, "end": v(-275.73, 40) * mm});
            skLineSegment(sketch, "E218.top", {"start": v(-295.73, 160) * mm, "end": v(-275.73, 160) * mm});
            skLineSegment(sketch, "E218.left", {"start": v(-295.73, 40) * mm, "end": v(-295.73, 100) * mm});
            skLineSegment(sketch, "E218.right", {"start": v(-275.73, 40) * mm, "end": v(-275.73, 60) * mm});
            skLineSegment(sketch, "E219.bottom", {"start": v(-275.73, 60) * mm, "end": v(-255.73, 60) * mm});
            skLineSegment(sketch, "E219.top", {"start": v(-275.73, 100) * mm, "end": v(-255.73, 100) * mm});
            skLineSegment(sketch, "E220.bottom", {"start": v(-295.73, 100) * mm, "end": v(-315.73, 100) * mm});
            skLineSegment(sketch, "E220.top", {"start": v(-295.73, 140) * mm, "end": v(-315.73, 140) * mm});
            skLineSegment(sketch, "E221.trimOffspring", {"start": v(-275.73, 100) * mm, "end": v(-275.73, 160) * mm});
            skLineSegment(sketch, "E222.trimOffspring", {"start": v(-295.73, 140) * mm, "end": v(-295.73, 160) * mm});
            skLineSegment(sketch, "E223", {"start": v(-315.73, 140) * mm, "end": v(-315.73, 100) * mm});
            skLineSegment(sketch, "E224", {"start": v(-255.73, 100) * mm, "end": v(-255.73, 60) * mm});
            skSolve(sketch);
        }
        {
            var Q0;
            Q0 = qSketchRegion(id + "F21", true);
            extrude(context, id + "F22", {"entities" : qUnion([Q0]), "operationType" : NewBodyOperationType.REMOVE, "endBound" : BoundingType.THROUGH_ALL, "oppositeDirection" : true, "depth" : 25 * mm});
        }
        {
            var Q0;
            Q0=qCreatedBy(makeId("Top.planeOp"),FACE);
            var sketch = newSketch(context, id + "F23", { "sketchPlane" : qUnion([Q0])});
            skPoint(sketch, "E225", {"position": v(-345.68, -334.18) * mm});
            skPoint(sketch, "E226.0.1.0", {"position": v(-345.68, -314.18) * mm});
            skPoint(sketch, "E226.0.2.0", {"position": v(-345.68, -294.18) * mm});
            skPoint(sketch, "E226.0.3.0", {"position": v(-345.68, -274.18) * mm});
            skPoint(sketch, "E226.0.4.0", {"position": v(-345.68, -254.18) * mm});
            skPoint(sketch, "E226.0.5.0", {"position": v(-345.68, -234.18) * mm});
            skPoint(sketch, "E226.0.6.0", {"position": v(-345.68, -214.18) * mm});
            skPoint(sketch, "E226.0.7.0", {"position": v(-345.68, -194.18) * mm});
            skPoint(sketch, "E226.0.8.0", {"position": v(-345.68, -174.18) * mm});
            skPoint(sketch, "E226.0.9.0", {"position": v(-345.68, -154.18) * mm});
            skPoint(sketch, "E226.0.10.0", {"position": v(-345.68, -134.18) * mm});
            skPoint(sketch, "E226.0.11.0", {"position": v(-345.68, -114.18) * mm});
            skPoint(sketch, "E226.0.12.0", {"position": v(-345.68, -94.18) * mm});
            skPoint(sketch, "E226.0.13.0", {"position": v(-345.68, -74.18) * mm});
            skPoint(sketch, "E226.1.0.0", {"position": v(-325.68, -334.18) * mm});
            skPoint(sketch, "E226.1.1.0", {"position": v(-325.68, -314.18) * mm});
            skPoint(sketch, "E226.1.2.0", {"position": v(-325.68, -294.18) * mm});
            skPoint(sketch, "E226.1.3.0", {"position": v(-325.68, -274.18) * mm});
            skPoint(sketch, "E226.1.4.0", {"position": v(-325.68, -254.18) * mm});
            skPoint(sketch, "E226.1.5.0", {"position": v(-325.68, -234.18) * mm});
            skPoint(sketch, "E226.1.6.0", {"position": v(-325.68, -214.18) * mm});
            skPoint(sketch, "E226.1.7.0", {"position": v(-325.68, -194.18) * mm});
            skPoint(sketch, "E226.1.8.0", {"position": v(-325.68, -174.18) * mm});
            skPoint(sketch, "E226.1.9.0", {"position": v(-325.68, -154.18) * mm});
            skPoint(sketch, "E226.1.10.0", {"position": v(-325.68, -134.18) * mm});
            skPoint(sketch, "E226.1.11.0", {"position": v(-325.68, -114.18) * mm});
            skPoint(sketch, "E226.1.12.0", {"position": v(-325.68, -94.18) * mm});
            skPoint(sketch, "E226.1.13.0", {"position": v(-325.68, -74.18) * mm});
            skPoint(sketch, "E226.2.0.0", {"position": v(-305.68, -334.18) * mm});
            skPoint(sketch, "E226.2.1.0", {"position": v(-305.68, -314.18) * mm});
            skPoint(sketch, "E226.2.2.0", {"position": v(-305.68, -294.18) * mm});
            skPoint(sketch, "E226.2.3.0", {"position": v(-305.68, -274.18) * mm});
            skPoint(sketch, "E226.2.4.0", {"position": v(-305.68, -254.18) * mm});
            skPoint(sketch, "E226.2.5.0", {"position": v(-305.68, -234.18) * mm});
            skPoint(sketch, "E226.2.6.0", {"position": v(-305.68, -214.18) * mm});
            skPoint(sketch, "E226.2.7.0", {"position": v(-305.68, -194.18) * mm});
            skPoint(sketch, "E226.2.8.0", {"position": v(-305.68, -174.18) * mm});
            skPoint(sketch, "E226.2.9.0", {"position": v(-305.68, -154.18) * mm});
            skPoint(sketch, "E226.2.10.0", {"position": v(-305.68, -134.18) * mm});
            skPoint(sketch, "E226.2.11.0", {"position": v(-305.68, -114.18) * mm});
            skPoint(sketch, "E226.2.12.0", {"position": v(-305.68, -94.18) * mm});
            skPoint(sketch, "E226.2.13.0", {"position": v(-305.68, -74.18) * mm});
            skPoint(sketch, "E226.3.0.0", {"position": v(-285.68, -334.18) * mm});
            skPoint(sketch, "E226.3.1.0", {"position": v(-285.68, -314.18) * mm});
            skPoint(sketch, "E226.3.2.0", {"position": v(-285.68, -294.18) * mm});
            skPoint(sketch, "E226.3.3.0", {"position": v(-285.68, -274.18) * mm});
            skPoint(sketch, "E226.3.4.0", {"position": v(-285.68, -254.18) * mm});
            skPoint(sketch, "E226.3.5.0", {"position": v(-285.68, -234.18) * mm});
            skPoint(sketch, "E226.3.6.0", {"position": v(-285.68, -214.18) * mm});
            skPoint(sketch, "E226.3.7.0", {"position": v(-285.68, -194.18) * mm});
            skPoint(sketch, "E226.3.8.0", {"position": v(-285.68, -174.18) * mm});
            skPoint(sketch, "E226.3.9.0", {"position": v(-285.68, -154.18) * mm});
            skPoint(sketch, "E226.3.10.0", {"position": v(-285.68, -134.18) * mm});
            skPoint(sketch, "E226.3.11.0", {"position": v(-285.68, -114.18) * mm});
            skPoint(sketch, "E226.3.12.0", {"position": v(-285.68, -94.18) * mm});
            skPoint(sketch, "E226.3.13.0", {"position": v(-285.68, -74.18) * mm});
            skPoint(sketch, "E226.4.0.0", {"position": v(-265.68, -334.18) * mm});
            skPoint(sketch, "E226.4.1.0", {"position": v(-265.68, -314.18) * mm});
            skPoint(sketch, "E226.4.2.0", {"position": v(-265.68, -294.18) * mm});
            skPoint(sketch, "E226.4.3.0", {"position": v(-265.68, -274.18) * mm});
            skPoint(sketch, "E226.4.4.0", {"position": v(-265.68, -254.18) * mm});
            skPoint(sketch, "E226.4.5.0", {"position": v(-265.68, -234.18) * mm});
            skPoint(sketch, "E226.4.6.0", {"position": v(-265.68, -214.18) * mm});
            skPoint(sketch, "E226.4.7.0", {"position": v(-265.68, -194.18) * mm});
            skPoint(sketch, "E226.4.8.0", {"position": v(-265.68, -174.18) * mm});
            skPoint(sketch, "E226.4.9.0", {"position": v(-265.68, -154.18) * mm});
            skPoint(sketch, "E226.4.10.0", {"position": v(-265.68, -134.18) * mm});
            skPoint(sketch, "E226.4.11.0", {"position": v(-265.68, -114.18) * mm});
            skPoint(sketch, "E226.4.12.0", {"position": v(-265.68, -94.18) * mm});
            skPoint(sketch, "E226.4.13.0", {"position": v(-265.68, -74.18) * mm});
            skPoint(sketch, "E226.5.0.0", {"position": v(-245.68, -334.18) * mm});
            skPoint(sketch, "E226.5.1.0", {"position": v(-245.68, -314.18) * mm});
            skPoint(sketch, "E226.5.2.0", {"position": v(-245.68, -294.18) * mm});
            skPoint(sketch, "E226.5.3.0", {"position": v(-245.68, -274.18) * mm});
            skPoint(sketch, "E226.5.4.0", {"position": v(-245.68, -254.18) * mm});
            skPoint(sketch, "E226.5.5.0", {"position": v(-245.68, -234.18) * mm});
            skPoint(sketch, "E226.5.6.0", {"position": v(-245.68, -214.18) * mm});
            skPoint(sketch, "E226.5.7.0", {"position": v(-245.68, -194.18) * mm});
            skPoint(sketch, "E226.5.8.0", {"position": v(-245.68, -174.18) * mm});
            skPoint(sketch, "E226.5.9.0", {"position": v(-245.68, -154.18) * mm});
            skPoint(sketch, "E226.5.10.0", {"position": v(-245.68, -134.18) * mm});
            skPoint(sketch, "E226.5.11.0", {"position": v(-245.68, -114.18) * mm});
            skPoint(sketch, "E226.5.12.0", {"position": v(-245.68, -94.18) * mm});
            skPoint(sketch, "E226.5.13.0", {"position": v(-245.68, -74.18) * mm});
            skPoint(sketch, "E226.6.0.0", {"position": v(-225.68, -334.18) * mm});
            skPoint(sketch, "E226.6.1.0", {"position": v(-225.68, -314.18) * mm});
            skPoint(sketch, "E226.6.2.0", {"position": v(-225.68, -294.18) * mm});
            skPoint(sketch, "E226.6.3.0", {"position": v(-225.68, -274.18) * mm});
            skPoint(sketch, "E226.6.4.0", {"position": v(-225.68, -254.18) * mm});
            skPoint(sketch, "E226.6.5.0", {"position": v(-225.68, -234.18) * mm});
            skPoint(sketch, "E226.6.6.0", {"position": v(-225.68, -214.18) * mm});
            skPoint(sketch, "E226.6.7.0", {"position": v(-225.68, -194.18) * mm});
            skPoint(sketch, "E226.6.8.0", {"position": v(-225.68, -174.18) * mm});
            skPoint(sketch, "E226.6.9.0", {"position": v(-225.68, -154.18) * mm});
            skPoint(sketch, "E226.6.10.0", {"position": v(-225.68, -134.18) * mm});
            skPoint(sketch, "E226.6.11.0", {"position": v(-225.68, -114.18) * mm});
            skPoint(sketch, "E226.6.12.0", {"position": v(-225.68, -94.18) * mm});
            skPoint(sketch, "E226.6.13.0", {"position": v(-225.68, -74.18) * mm});
            skPoint(sketch, "E226.7.0.0", {"position": v(-205.68, -334.18) * mm});
            skPoint(sketch, "E226.7.1.0", {"position": v(-205.68, -314.18) * mm});
            skPoint(sketch, "E226.7.2.0", {"position": v(-205.68, -294.18) * mm});
            skPoint(sketch, "E226.7.3.0", {"position": v(-205.68, -274.18) * mm});
            skPoint(sketch, "E226.7.4.0", {"position": v(-205.68, -254.18) * mm});
            skPoint(sketch, "E226.7.5.0", {"position": v(-205.68, -234.18) * mm});
            skPoint(sketch, "E226.7.6.0", {"position": v(-205.68, -214.18) * mm});
            skPoint(sketch, "E226.7.7.0", {"position": v(-205.68, -194.18) * mm});
            skPoint(sketch, "E226.7.8.0", {"position": v(-205.68, -174.18) * mm});
            skPoint(sketch, "E226.7.9.0", {"position": v(-205.68, -154.18) * mm});
            skPoint(sketch, "E226.7.10.0", {"position": v(-205.68, -134.18) * mm});
            skPoint(sketch, "E226.7.11.0", {"position": v(-205.68, -114.18) * mm});
            skPoint(sketch, "E226.7.12.0", {"position": v(-205.68, -94.18) * mm});
            skPoint(sketch, "E226.7.13.0", {"position": v(-205.68, -74.18) * mm});
            skPoint(sketch, "E226.8.0.0", {"position": v(-185.68, -334.18) * mm});
            skPoint(sketch, "E226.8.1.0", {"position": v(-185.68, -314.18) * mm});
            skPoint(sketch, "E226.8.2.0", {"position": v(-185.68, -294.18) * mm});
            skPoint(sketch, "E226.8.3.0", {"position": v(-185.68, -274.18) * mm});
            skPoint(sketch, "E226.8.4.0", {"position": v(-185.68, -254.18) * mm});
            skPoint(sketch, "E226.8.5.0", {"position": v(-185.68, -234.18) * mm});
            skPoint(sketch, "E226.8.6.0", {"position": v(-185.68, -214.18) * mm});
            skPoint(sketch, "E226.8.7.0", {"position": v(-185.68, -194.18) * mm});
            skPoint(sketch, "E226.8.8.0", {"position": v(-185.68, -174.18) * mm});
            skPoint(sketch, "E226.8.9.0", {"position": v(-185.68, -154.18) * mm});
            skPoint(sketch, "E226.8.10.0", {"position": v(-185.68, -134.18) * mm});
            skPoint(sketch, "E226.8.11.0", {"position": v(-185.68, -114.18) * mm});
            skPoint(sketch, "E226.8.12.0", {"position": v(-185.68, -94.18) * mm});
            skPoint(sketch, "E226.8.13.0", {"position": v(-185.68, -74.18) * mm});
            skPoint(sketch, "E226.9.0.0", {"position": v(-165.68, -334.18) * mm});
            skPoint(sketch, "E226.9.1.0", {"position": v(-165.68, -314.18) * mm});
            skPoint(sketch, "E226.9.2.0", {"position": v(-165.68, -294.18) * mm});
            skPoint(sketch, "E226.9.3.0", {"position": v(-165.68, -274.18) * mm});
            skPoint(sketch, "E226.9.4.0", {"position": v(-165.68, -254.18) * mm});
            skPoint(sketch, "E226.9.5.0", {"position": v(-165.68, -234.18) * mm});
            skPoint(sketch, "E226.9.6.0", {"position": v(-165.68, -214.18) * mm});
            skPoint(sketch, "E226.9.7.0", {"position": v(-165.68, -194.18) * mm});
            skPoint(sketch, "E226.9.8.0", {"position": v(-165.68, -174.18) * mm});
            skPoint(sketch, "E226.9.9.0", {"position": v(-165.68, -154.18) * mm});
            skPoint(sketch, "E226.9.10.0", {"position": v(-165.68, -134.18) * mm});
            skPoint(sketch, "E226.9.11.0", {"position": v(-165.68, -114.18) * mm});
            skPoint(sketch, "E226.9.12.0", {"position": v(-165.68, -94.18) * mm});
            skPoint(sketch, "E226.9.13.0", {"position": v(-165.68, -74.18) * mm});
            skPoint(sketch, "E226.10.0.0", {"position": v(-145.68, -334.18) * mm});
            skPoint(sketch, "E226.10.1.0", {"position": v(-145.68, -314.18) * mm});
            skPoint(sketch, "E226.10.2.0", {"position": v(-145.68, -294.18) * mm});
            skPoint(sketch, "E226.10.3.0", {"position": v(-145.68, -274.18) * mm});
            skPoint(sketch, "E226.10.4.0", {"position": v(-145.68, -254.18) * mm});
            skPoint(sketch, "E226.10.5.0", {"position": v(-145.68, -234.18) * mm});
            skPoint(sketch, "E226.10.6.0", {"position": v(-145.68, -214.18) * mm});
            skPoint(sketch, "E226.10.7.0", {"position": v(-145.68, -194.18) * mm});
            skPoint(sketch, "E226.10.8.0", {"position": v(-145.68, -174.18) * mm});
            skPoint(sketch, "E226.10.9.0", {"position": v(-145.68, -154.18) * mm});
            skPoint(sketch, "E226.10.10.0", {"position": v(-145.68, -134.18) * mm});
            skPoint(sketch, "E226.10.11.0", {"position": v(-145.68, -114.18) * mm});
            skPoint(sketch, "E226.10.12.0", {"position": v(-145.68, -94.18) * mm});
            skPoint(sketch, "E226.10.13.0", {"position": v(-145.68, -74.18) * mm});
            skPoint(sketch, "E226.11.0.0", {"position": v(-125.68, -334.18) * mm});
            skPoint(sketch, "E226.11.1.0", {"position": v(-125.68, -314.18) * mm});
            skPoint(sketch, "E226.11.2.0", {"position": v(-125.68, -294.18) * mm});
            skPoint(sketch, "E226.11.3.0", {"position": v(-125.68, -274.18) * mm});
            skPoint(sketch, "E226.11.4.0", {"position": v(-125.68, -254.18) * mm});
            skPoint(sketch, "E226.11.5.0", {"position": v(-125.68, -234.18) * mm});
            skPoint(sketch, "E226.11.6.0", {"position": v(-125.68, -214.18) * mm});
            skPoint(sketch, "E226.11.7.0", {"position": v(-125.68, -194.18) * mm});
            skPoint(sketch, "E226.11.8.0", {"position": v(-125.68, -174.18) * mm});
            skPoint(sketch, "E226.11.9.0", {"position": v(-125.68, -154.18) * mm});
            skPoint(sketch, "E226.11.10.0", {"position": v(-125.68, -134.18) * mm});
            skPoint(sketch, "E226.11.11.0", {"position": v(-125.68, -114.18) * mm});
            skPoint(sketch, "E226.11.12.0", {"position": v(-125.68, -94.18) * mm});
            skPoint(sketch, "E226.11.13.0", {"position": v(-125.68, -74.18) * mm});
            skPoint(sketch, "E226.12.0.0", {"position": v(-105.68, -334.18) * mm});
            skPoint(sketch, "E226.12.1.0", {"position": v(-105.68, -314.18) * mm});
            skPoint(sketch, "E226.12.2.0", {"position": v(-105.68, -294.18) * mm});
            skPoint(sketch, "E226.12.3.0", {"position": v(-105.68, -274.18) * mm});
            skPoint(sketch, "E226.12.4.0", {"position": v(-105.68, -254.18) * mm});
            skPoint(sketch, "E226.12.5.0", {"position": v(-105.68, -234.18) * mm});
            skPoint(sketch, "E226.12.6.0", {"position": v(-105.68, -214.18) * mm});
            skPoint(sketch, "E226.12.7.0", {"position": v(-105.68, -194.18) * mm});
            skPoint(sketch, "E226.12.8.0", {"position": v(-105.68, -174.18) * mm});
            skPoint(sketch, "E226.12.9.0", {"position": v(-105.68, -154.18) * mm});
            skPoint(sketch, "E226.12.10.0", {"position": v(-105.68, -134.18) * mm});
            skPoint(sketch, "E226.12.11.0", {"position": v(-105.68, -114.18) * mm});
            skPoint(sketch, "E226.12.12.0", {"position": v(-105.68, -94.18) * mm});
            skPoint(sketch, "E226.12.13.0", {"position": v(-105.68, -74.18) * mm});
            skPoint(sketch, "E226.13.0.0", {"position": v(-85.68, -334.18) * mm});
            skPoint(sketch, "E226.13.1.0", {"position": v(-85.68, -314.18) * mm});
            skPoint(sketch, "E226.13.2.0", {"position": v(-85.68, -294.18) * mm});
            skPoint(sketch, "E226.13.3.0", {"position": v(-85.68, -274.18) * mm});
            skPoint(sketch, "E226.13.4.0", {"position": v(-85.68, -254.18) * mm});
            skPoint(sketch, "E226.13.5.0", {"position": v(-85.68, -234.18) * mm});
            skPoint(sketch, "E226.13.6.0", {"position": v(-85.68, -214.18) * mm});
            skPoint(sketch, "E226.13.7.0", {"position": v(-85.68, -194.18) * mm});
            skPoint(sketch, "E226.13.8.0", {"position": v(-85.68, -174.18) * mm});
            skPoint(sketch, "E226.13.9.0", {"position": v(-85.68, -154.18) * mm});
            skPoint(sketch, "E226.13.10.0", {"position": v(-85.68, -134.18) * mm});
            skPoint(sketch, "E226.13.11.0", {"position": v(-85.68, -114.18) * mm});
            skPoint(sketch, "E226.13.12.0", {"position": v(-85.68, -94.18) * mm});
            skPoint(sketch, "E226.13.13.0", {"position": v(-85.68, -74.18) * mm});
            skLineSegment(sketch, "E226.direction1", {"start": v(-345.68, -334.18) * mm, "end": v(-325.68, -334.18) * mm, "construction": true});
            skLineSegment(sketch, "E226.direction2", {"start": v(-345.68, -334.18) * mm, "end": v(-345.68, -314.18) * mm, "construction": true});
            skPoint(sketch, "E227.0.0.14", {"position": v(-345.68, -54.18) * mm});
            skPoint(sketch, "E227.0.1.14", {"position": v(-325.68, -54.18) * mm});
            skPoint(sketch, "E227.0.2.14", {"position": v(-305.68, -54.18) * mm});
            skPoint(sketch, "E227.0.3.14", {"position": v(-285.68, -54.18) * mm});
            skPoint(sketch, "E227.0.4.14", {"position": v(-265.68, -54.18) * mm});
            skPoint(sketch, "E227.0.5.14", {"position": v(-245.68, -54.18) * mm});
            skPoint(sketch, "E227.0.6.14", {"position": v(-225.68, -54.18) * mm});
            skPoint(sketch, "E227.0.7.14", {"position": v(-205.68, -54.18) * mm});
            skPoint(sketch, "E227.0.8.14", {"position": v(-185.68, -54.18) * mm});
            skPoint(sketch, "E227.0.9.14", {"position": v(-165.68, -54.18) * mm});
            skPoint(sketch, "E227.0.10.14", {"position": v(-145.68, -54.18) * mm});
            skPoint(sketch, "E227.0.11.14", {"position": v(-125.68, -54.18) * mm});
            skPoint(sketch, "E227.0.12.14", {"position": v(-105.68, -54.18) * mm});
            skPoint(sketch, "E227.0.13.14", {"position": v(-85.68, -54.18) * mm});
            skPoint(sketch, "E228.0.14.0", {"position": v(-65.68, -334.18) * mm});
            skPoint(sketch, "E228.0.14.1", {"position": v(-65.68, -314.18) * mm});
            skPoint(sketch, "E228.0.14.2", {"position": v(-65.68, -294.18) * mm});
            skPoint(sketch, "E228.0.14.3", {"position": v(-65.68, -274.18) * mm});
            skPoint(sketch, "E228.0.14.4", {"position": v(-65.68, -254.18) * mm});
            skPoint(sketch, "E228.0.14.5", {"position": v(-65.68, -234.18) * mm});
            skPoint(sketch, "E228.0.14.6", {"position": v(-65.68, -214.18) * mm});
            skPoint(sketch, "E228.0.14.7", {"position": v(-65.68, -194.18) * mm});
            skPoint(sketch, "E228.0.14.8", {"position": v(-65.68, -174.18) * mm});
            skPoint(sketch, "E228.0.14.9", {"position": v(-65.68, -154.18) * mm});
            skPoint(sketch, "E228.0.14.10", {"position": v(-65.68, -134.18) * mm});
            skPoint(sketch, "E228.0.14.11", {"position": v(-65.68, -114.18) * mm});
            skPoint(sketch, "E228.0.14.12", {"position": v(-65.68, -94.18) * mm});
            skPoint(sketch, "E228.0.14.13", {"position": v(-65.68, -74.18) * mm});
            skPoint(sketch, "E228.0.14.14", {"position": v(-65.68, -54.18) * mm});
            skLineSegment(sketch, "E229", {"start": v(-325.68, -254.18) * mm, "end": v(-325.68, -274.18) * mm});
            skLineSegment(sketch, "E230", {"start": v(-325.68, -274.18) * mm, "end": v(-305.68, -274.18) * mm});
            skLineSegment(sketch, "E231", {"start": v(-305.68, -274.18) * mm, "end": v(-305.68, -254.18) * mm});
            skLineSegment(sketch, "E232", {"start": v(-305.68, -254.18) * mm, "end": v(-325.68, -254.18) * mm});
            skLineSegment(sketch, "E233", {"start": v(-285.68, -174.18) * mm, "end": v(-285.68, -214.18) * mm});
            skLineSegment(sketch, "E234", {"start": v(-285.68, -174.18) * mm, "end": v(-305.68, -174.18) * mm});
            skLineSegment(sketch, "E235", {"start": v(-305.68, -174.18) * mm, "end": v(-305.68, -214.18) * mm});
            skLineSegment(sketch, "E236", {"start": v(-285.68, -214.18) * mm, "end": v(-305.68, -214.18) * mm});
            skLineSegment(sketch, "E237.bottom", {"start": v(-305.68, -114.18) * mm, "end": v(-325.68, -114.18) * mm});
            skLineSegment(sketch, "E237.top", {"start": v(-305.68, -74.18) * mm, "end": v(-325.68, -74.18) * mm});
            skLineSegment(sketch, "E237.left", {"start": v(-305.68, -114.18) * mm, "end": v(-305.68, -74.18) * mm});
            skLineSegment(sketch, "E237.right", {"start": v(-325.68, -114.18) * mm, "end": v(-325.68, -74.18) * mm});
            skLineSegment(sketch, "E238", {"start": v(-265.68, -214.18) * mm, "end": v(-245.68, -214.18) * mm});
            skLineSegment(sketch, "E239", {"start": v(-245.68, -214.18) * mm, "end": v(-245.68, -194.18) * mm});
            skLineSegment(sketch, "E240", {"start": v(-225.68, -194.18) * mm, "end": v(-245.68, -194.18) * mm});
            skLineSegment(sketch, "E241", {"start": v(-265.68, -214.18) * mm, "end": v(-265.68, -254.18) * mm});
            skLineSegment(sketch, "E242", {"start": v(-225.68, -194.18) * mm, "end": v(-225.68, -294.18) * mm});
            skLineSegment(sketch, "E243", {"start": v(-265.68, -254.18) * mm, "end": v(-245.68, -254.18) * mm});
            skLineSegment(sketch, "E244", {"start": v(-245.68, -254.18) * mm, "end": v(-245.68, -294.18) * mm});
            skLineSegment(sketch, "E245", {"start": v(-225.68, -294.18) * mm, "end": v(-245.68, -294.18) * mm});
            skLineSegment(sketch, "E246.bottom", {"start": v(-205.68, -294.18) * mm, "end": v(-185.68, -294.18) * mm});
            skLineSegment(sketch, "E246.top", {"start": v(-205.68, -334.18) * mm, "end": v(-185.68, -334.18) * mm});
            skLineSegment(sketch, "E246.left", {"start": v(-205.68, -294.18) * mm, "end": v(-205.68, -334.18) * mm});
            skLineSegment(sketch, "E246.right", {"start": v(-185.68, -294.18) * mm, "end": v(-185.68, -334.18) * mm});
            skLineSegment(sketch, "E247.bottom", {"start": v(-165.68, -274.18) * mm, "end": v(-145.68, -274.18) * mm});
            skLineSegment(sketch, "E247.top", {"start": v(-165.68, -254.18) * mm, "end": v(-145.68, -254.18) * mm});
            skLineSegment(sketch, "E247.left", {"start": v(-165.68, -274.18) * mm, "end": v(-165.68, -254.18) * mm});
            skLineSegment(sketch, "E247.right", {"start": v(-145.68, -274.18) * mm, "end": v(-145.68, -254.18) * mm});
            skLineSegment(sketch, "E248", {"start": v(-185.68, -194.18) * mm, "end": v(-205.68, -194.18) * mm});
            skLineSegment(sketch, "E249", {"start": v(-185.68, -194.18) * mm, "end": v(-185.68, -214.18) * mm});
            skLineSegment(sketch, "E250", {"start": v(-185.68, -214.18) * mm, "end": v(-165.68, -214.18) * mm});
            skLineSegment(sketch, "E251", {"start": v(-205.68, -194.18) * mm, "end": v(-205.68, -154.18) * mm});
            skLineSegment(sketch, "E252", {"start": v(-205.68, -154.18) * mm, "end": v(-185.68, -154.18) * mm});
            skLineSegment(sketch, "E253", {"start": v(-165.68, -214.18) * mm, "end": v(-165.68, -134.18) * mm});
            skLineSegment(sketch, "E254", {"start": v(-165.68, -134.18) * mm, "end": v(-185.68, -134.18) * mm});
            skLineSegment(sketch, "E255", {"start": v(-185.68, -134.18) * mm, "end": v(-185.68, -154.18) * mm});
            skLineSegment(sketch, "E256.bottom", {"start": v(-225.68, -154.18) * mm, "end": v(-265.68, -154.18) * mm});
            skLineSegment(sketch, "E256.top", {"start": v(-225.68, -114.18) * mm, "end": v(-265.68, -114.18) * mm});
            skLineSegment(sketch, "E256.left", {"start": v(-225.68, -154.18) * mm, "end": v(-225.68, -114.18) * mm});
            skLineSegment(sketch, "E256.right", {"start": v(-265.68, -154.18) * mm, "end": v(-265.68, -114.18) * mm});
            skLineSegment(sketch, "E257.bottom", {"start": v(-105.68, -74.18) * mm, "end": v(-125.68, -74.18) * mm});
            skLineSegment(sketch, "E257.top", {"start": v(-105.68, -194.18) * mm, "end": v(-125.68, -194.18) * mm});
            skLineSegment(sketch, "E257.left", {"start": v(-105.68, -74.18) * mm, "end": v(-105.68, -134.18) * mm});
            skLineSegment(sketch, "E257.right", {"start": v(-125.68, -74.18) * mm, "end": v(-125.68, -94.18) * mm});
            skLineSegment(sketch, "E258.bottom", {"start": v(-125.68, -94.18) * mm, "end": v(-145.68, -94.18) * mm});
            skLineSegment(sketch, "E258.top", {"start": v(-125.68, -134.18) * mm, "end": v(-145.68, -134.18) * mm});
            skLineSegment(sketch, "E259.bottom", {"start": v(-105.68, -134.18) * mm, "end": v(-85.68, -134.18) * mm});
            skLineSegment(sketch, "E259.top", {"start": v(-105.68, -174.18) * mm, "end": v(-85.68, -174.18) * mm});
            skLineSegment(sketch, "E260.trimOffspring", {"start": v(-125.68, -134.18) * mm, "end": v(-125.68, -194.18) * mm});
            skLineSegment(sketch, "E261.trimOffspring", {"start": v(-105.68, -174.18) * mm, "end": v(-105.68, -194.18) * mm});
            skLineSegment(sketch, "E262", {"start": v(-85.68, -134.18) * mm, "end": v(-85.68, -174.18) * mm});
            skLineSegment(sketch, "E263", {"start": v(-145.68, -94.18) * mm, "end": v(-145.68, -134.18) * mm});
            skSolve(sketch);
        }
        {
            var Q0;
            Q0 = qSketchRegion(id + "F23", true);
            extrude(context, id + "F24", {"entities" : qUnion([Q0]), "depth" : 3 * mm});
        }
    });
